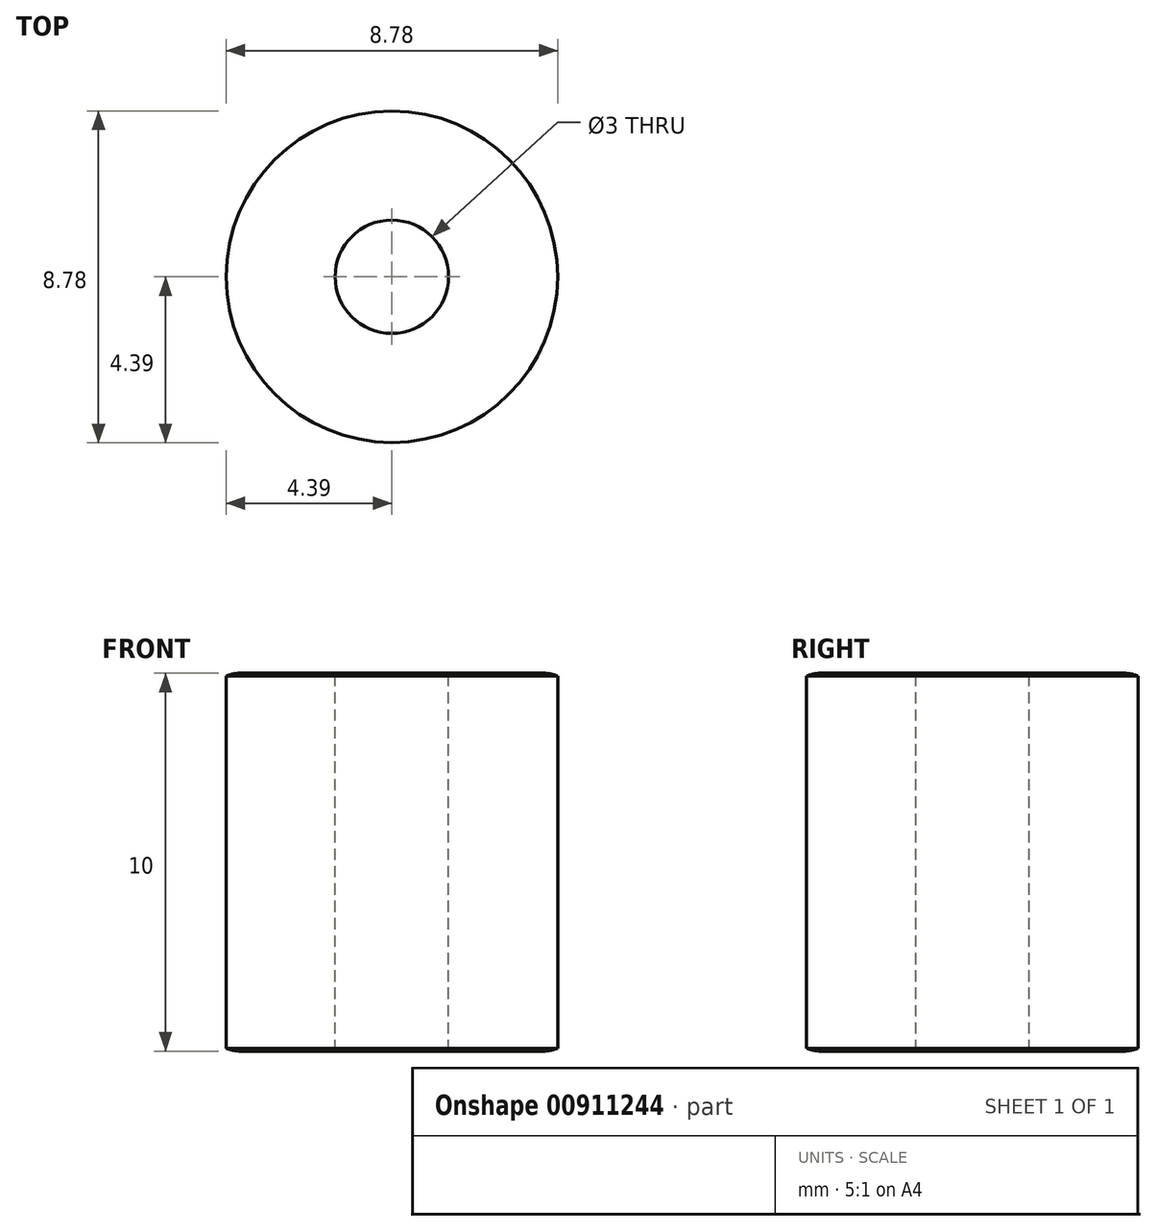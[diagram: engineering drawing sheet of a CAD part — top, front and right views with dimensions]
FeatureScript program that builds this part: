
annotation { "Feature Type Name" : "Feature", "Feature Type Description" : "" }
export const myFeature = defineFeature(function(context is Context, id is Id, definition is map)
    precondition{}
    {
        {
            var Q0;
            Q0=qCreatedBy(makeId("Top.planeOp"),FACE);
            var sketch = newSketch(context, id + "F0", { "sketchPlane" : qUnion([Q0])});
            skCircle(sketch, "E0", {"center": v(0, 0) * mm, "radius": 40 * mm});
            skCircle(sketch, "E1", {"center": v(0, 0) * mm, "radius": 35 * mm});
            skSolve(sketch);
        }
        {
            var Q0;
            Q0=qSketchRegion(id+"F0",true);
            extrude(context, id + "F1", {"entities" : qUnion([Q0]), "depth" : 10 * mm, "offsetDistance" : 25 * mm, "symmetric" : true});
        }
        {
            var Q0;
            Q0=makeQuery(id+"F1.opExtrude","CAP_EDGE",EDGE,{"disambiguationData":[OSD([sQuery(id+"F0.wireOp",EDGE,"E0")])],"isStart":false});
            var Q1;
            Q1=makeQuery(id+"F1.opExtrude","CAP_EDGE",EDGE,{"disambiguationData":[OSD([sQuery(id+"F0.wireOp",EDGE,"E0")])],"isStart":true});
            fillet(context, id + "F2", {"entities" : qUnion([Q0, Q1]), "radius" : 5 * mm, "tangentPropagation" : true, "allowEdgeOverflow" : false});
        }
        {
            var Q0;
            Q0=makeQuery(id+"F0.imprint","IMPRINT",FACE,{"disambiguationData":[TD([[makeQuery(id+"F0.imprint","IMPRINT",EDGE,{"derivedFrom":sQuery(id+"F0.wireOp",EDGE,"E1")}),1.0]])]});
            extrude(context, id + "F3", {"entities" : qUnion([Q0]), "operationType" : NewBodyOperationType.ADD, "depth" : 5 * mm, "offsetDistance" : 25 * mm, "symmetric" : true});
        }
        {
            var Q0;
            Q0=qCreatedBy(makeId("Top.planeOp"),FACE);
            var sketch = newSketch(context, id + "F4", { "sketchPlane" : qUnion([Q0])});
            skCircle(sketch, "E2", {"center": v(0, 0) * mm, "radius": 5 * mm});
            skSolve(sketch);
        }
        {
            var Q0;
            Q0=qSketchRegion(id+"F4",true);
            extrude(context, id + "F5", {"entities" : qUnion([Q0]), "operationType" : NewBodyOperationType.ADD, "depth" : 10 * mm, "offsetDistance" : 25 * mm, "symmetric" : true});
        }
        {
            var Q0;
            Q0=qCreatedBy(makeId("Top.planeOp"),FACE);
            var sketch = newSketch(context, id + "F6", { "sketchPlane" : qUnion([Q0])});
            skCircle(sketch, "E3", {"center": v(0, 0) * mm, "radius": 1.5 * mm});
            skSolve(sketch);
        }
        {
            var Q0;
            Q0=qSketchRegion(id+"F6",true);
            extrude(context, id + "F7", {"entities" : qUnion([Q0]), "operationType" : NewBodyOperationType.REMOVE, "oppositeDirection" : true, "depth" : 10 * mm, "offsetDistance" : 25 * mm, "symmetric" : true});
        }
        {
            var Q0;
            Q0=qCreatedBy(makeId("Top.planeOp"),FACE);
            var sketch = newSketch(context, id + "F8", { "sketchPlane" : qUnion([Q0])});
            skArc(sketch, "E4", {"start": v(-31.79, 5.48) * mm, "mid": v(-31.09, 8.72) * mm, "end": v(-30.01, 11.86) * mm});
            skLineSegment(sketch, "E5", {"start": v(-27.27, 12.9) * mm, "end": v(-8.35, 3.42) * mm});
            skLineSegment(sketch, "E6", {"start": v(-29.97, 3.18) * mm, "end": v(-8.88, 1.53) * mm});
            skArc(sketch, "E7.filletArc", {"start": v(-8.88, 1.53) * mm, "mid": v(-7.83, 2.26) * mm, "end": v(-8.35, 3.42) * mm});
            skPoint(sketch, "E8.visualSharp", {"position": v(-29.12, 13.82) * mm});
            skArc(sketch, "E8.filletArc", {"start": v(-27.27, 12.9) * mm, "mid": v(-28.87, 12.97) * mm, "end": v(-30.01, 11.86) * mm});
            skPoint(sketch, "E9.visualSharp", {"position": v(-32.04, 3.34) * mm});
            skArc(sketch, "E9.filletArc", {"start": v(-31.79, 5.48) * mm, "mid": v(-31.38, 3.93) * mm, "end": v(-29.97, 3.18) * mm});
            skPoint(sketch, "E10.1.0", {"position": v(-29.54, -13.16) * mm});
            skLineSegment(sketch, "E10.1.1", {"start": v(-27.66, -12.26) * mm, "end": v(-8.58, -3.14) * mm});
            skArc(sketch, "E10.1.2", {"start": v(-8.58, -3.14) * mm, "mid": v(-8.04, -1.99) * mm, "end": v(-9.07, -1.24) * mm});
            skLineSegment(sketch, "E10.1.3", {"start": v(-30.18, -2.5) * mm, "end": v(-9.07, -1.24) * mm});
            skPoint(sketch, "E10.1.4", {"position": v(-32.25, -2.63) * mm});
            skArc(sketch, "E10.1.5", {"start": v(-30.4, -11.18) * mm, "mid": v(-31.4, -8.02) * mm, "end": v(-32.05, -4.77) * mm});
            skArc(sketch, "E10.1.6", {"start": v(-30.18, -2.5) * mm, "mid": v(-31.6, -3.23) * mm, "end": v(-32.05, -4.77) * mm});
            skArc(sketch, "E10.1.7", {"start": v(-30.4, -11.18) * mm, "mid": v(-29.26, -12.32) * mm, "end": v(-27.66, -12.26) * mm});
            skPoint(sketch, "E10.2.0", {"position": v(-19.12, -26.2) * mm});
            skLineSegment(sketch, "E10.2.1", {"start": v(-17.95, -24.48) * mm, "end": v(-5.98, -7.04) * mm});
            skArc(sketch, "E10.2.2", {"start": v(-5.98, -7.04) * mm, "mid": v(-6.09, -5.77) * mm, "end": v(-7.35, -5.64) * mm});
            skLineSegment(sketch, "E10.2.3", {"start": v(-25.01, -17.29) * mm, "end": v(-7.35, -5.64) * mm});
            skPoint(sketch, "E10.2.4", {"position": v(-26.74, -18.43) * mm});
            skArc(sketch, "E10.2.5", {"start": v(-20.85, -24.9) * mm, "mid": v(-23.3, -22.68) * mm, "end": v(-25.5, -20.18) * mm});
            skArc(sketch, "E10.2.6", {"start": v(-25.01, -17.29) * mm, "mid": v(-25.88, -18.63) * mm, "end": v(-25.5, -20.18) * mm});
            skArc(sketch, "E10.2.7", {"start": v(-20.85, -24.9) * mm, "mid": v(-19.3, -25.33) * mm, "end": v(-17.95, -24.48) * mm});
            skPoint(sketch, "E10.center", {"position": v(0, -0.25) * mm});
            skPoint(sketch, "E11.0.3.0", {"position": v(-14.07, -29.37) * mm});
            skLineSegment(sketch, "E11.1.3.0", {"start": v(-3.43, -30.2) * mm, "end": v(-1.78, -9.12) * mm});
            skArc(sketch, "E11.4.3.0", {"start": v(-1.78, -9.12) * mm, "mid": v(-2.5, -8.08) * mm, "end": v(-3.67, -8.6) * mm});
            skLineSegment(sketch, "E11.8.3.0", {"start": v(-13.14, -27.5) * mm, "end": v(-3.67, -8.6) * mm});
            skPoint(sketch, "E11.11.3.0", {"position": v(-3.59, -32.28) * mm});
            skArc(sketch, "E11.12.3.0", {"start": v(-5.73, -32.03) * mm, "mid": v(-8.97, -31.33) * mm, "end": v(-12.1, -30.26) * mm});
            skArc(sketch, "E11.16.3.0", {"start": v(-13.14, -27.5) * mm, "mid": v(-13.22, -29.1) * mm, "end": v(-12.1, -30.26) * mm});
            skArc(sketch, "E11.20.3.0", {"start": v(-5.73, -32.03) * mm, "mid": v(-4.18, -31.62) * mm, "end": v(-3.43, -30.2) * mm});
            skPoint(sketch, "E11.0.4.0", {"position": v(2.38, -32.5) * mm});
            skLineSegment(sketch, "E11.1.4.0", {"start": v(12.01, -27.9) * mm, "end": v(2.9, -8.82) * mm});
            skArc(sketch, "E11.4.4.0", {"start": v(2.9, -8.82) * mm, "mid": v(1.74, -8.28) * mm, "end": v(1, -9.3) * mm});
            skLineSegment(sketch, "E11.8.4.0", {"start": v(2.25, -30.42) * mm, "end": v(1, -9.3) * mm});
            skPoint(sketch, "E11.11.4.0", {"position": v(12.9, -29.78) * mm});
            skArc(sketch, "E11.12.4.0", {"start": v(10.93, -30.63) * mm, "mid": v(7.77, -31.65) * mm, "end": v(4.52, -32.29) * mm});
            skArc(sketch, "E11.16.4.0", {"start": v(2.25, -30.42) * mm, "mid": v(2.98, -31.85) * mm, "end": v(4.52, -32.29) * mm});
            skArc(sketch, "E11.20.4.0", {"start": v(10.93, -30.63) * mm, "mid": v(12.07, -29.5) * mm, "end": v(12.01, -27.9) * mm});
            skPoint(sketch, "E12.0.5.0", {"position": v(18.18, -26.99) * mm});
            skLineSegment(sketch, "E12.1.5.0", {"start": v(24.23, -18.2) * mm, "end": v(6.8, -6.22) * mm});
            skArc(sketch, "E12.4.5.0", {"start": v(6.8, -6.22) * mm, "mid": v(5.53, -6.33) * mm, "end": v(5.4, -7.6) * mm});
            skLineSegment(sketch, "E12.8.5.0", {"start": v(17.04, -25.25) * mm, "end": v(5.4, -7.6) * mm});
            skPoint(sketch, "E12.11.5.0", {"position": v(25.94, -19.37) * mm});
            skArc(sketch, "E12.12.5.0", {"start": v(24.66, -21.1) * mm, "mid": v(22.43, -23.55) * mm, "end": v(19.94, -25.73) * mm});
            skArc(sketch, "E12.16.5.0", {"start": v(17.04, -25.25) * mm, "mid": v(18.38, -26.12) * mm, "end": v(19.94, -25.73) * mm});
            skArc(sketch, "E12.20.5.0", {"start": v(24.66, -21.1) * mm, "mid": v(25.08, -19.55) * mm, "end": v(24.23, -18.2) * mm});
            skPoint(sketch, "E13.0.6.0", {"position": v(29.12, -14.3) * mm});
            skLineSegment(sketch, "E13.1.6.0", {"start": v(29.96, -3.67) * mm, "end": v(8.87, -2.02) * mm});
            skArc(sketch, "E13.4.6.0", {"start": v(8.87, -2.02) * mm, "mid": v(7.83, -2.75) * mm, "end": v(8.34, -3.91) * mm});
            skLineSegment(sketch, "E13.8.6.0", {"start": v(27.26, -13.38) * mm, "end": v(8.34, -3.91) * mm});
            skPoint(sketch, "E13.11.6.0", {"position": v(32.03, -3.83) * mm});
            skArc(sketch, "E13.12.6.0", {"start": v(31.78, -5.97) * mm, "mid": v(31.08, -9.21) * mm, "end": v(30, -12.35) * mm});
            skArc(sketch, "E13.16.6.0", {"start": v(27.26, -13.38) * mm, "mid": v(28.86, -13.46) * mm, "end": v(30, -12.35) * mm});
            skArc(sketch, "E13.20.6.0", {"start": v(31.78, -5.97) * mm, "mid": v(31.37, -4.42) * mm, "end": v(29.96, -3.67) * mm});
            skPoint(sketch, "E14.0.7.0", {"position": v(32.25, 2.14) * mm});
            skLineSegment(sketch, "E14.1.7.0", {"start": v(27.66, 11.77) * mm, "end": v(8.57, 2.65) * mm});
            skArc(sketch, "E14.4.7.0", {"start": v(8.57, 2.65) * mm, "mid": v(8.03, 1.5) * mm, "end": v(9.06, 0.75) * mm});
            skLineSegment(sketch, "E14.8.7.0", {"start": v(30.18, 2.01) * mm, "end": v(9.06, 0.75) * mm});
            skPoint(sketch, "E14.11.7.0", {"position": v(29.53, 12.67) * mm});
            skArc(sketch, "E14.12.7.0", {"start": v(30.38, 10.69) * mm, "mid": v(31.4, 7.53) * mm, "end": v(32.04, 4.28) * mm});
            skArc(sketch, "E14.16.7.0", {"start": v(30.18, 2.01) * mm, "mid": v(31.6, 2.74) * mm, "end": v(32.04, 4.28) * mm});
            skArc(sketch, "E14.20.7.0", {"start": v(30.38, 10.69) * mm, "mid": v(29.26, 11.83) * mm, "end": v(27.66, 11.77) * mm});
            skPoint(sketch, "E15.0.8.0", {"position": v(26.74, 17.94) * mm});
            skLineSegment(sketch, "E15.1.8.0", {"start": v(17.94, 24) * mm, "end": v(5.97, 6.55) * mm});
            skArc(sketch, "E15.4.8.0", {"start": v(5.97, 6.55) * mm, "mid": v(6.08, 5.28) * mm, "end": v(7.35, 5.15) * mm});
            skLineSegment(sketch, "E15.8.8.0", {"start": v(25, 16.8) * mm, "end": v(7.35, 5.15) * mm});
            skPoint(sketch, "E15.11.8.0", {"position": v(19.12, 25.7) * mm});
            skArc(sketch, "E15.12.8.0", {"start": v(20.85, 24.42) * mm, "mid": v(23.3, 22.2) * mm, "end": v(25.48, 19.7) * mm});
            skArc(sketch, "E15.16.8.0", {"start": v(25, 16.8) * mm, "mid": v(25.88, 18.14) * mm, "end": v(25.48, 19.7) * mm});
            skArc(sketch, "E15.20.8.0", {"start": v(20.85, 24.42) * mm, "mid": v(19.3, 24.84) * mm, "end": v(17.94, 24) * mm});
            skPoint(sketch, "E15.0.9.0", {"position": v(14.06, 28.88) * mm});
            skLineSegment(sketch, "E15.1.9.0", {"start": v(3.42, 29.72) * mm, "end": v(1.77, 8.63) * mm});
            skArc(sketch, "E15.4.9.0", {"start": v(1.77, 8.63) * mm, "mid": v(2.5, 7.59) * mm, "end": v(3.67, 8.1) * mm});
            skLineSegment(sketch, "E15.8.9.0", {"start": v(13.13, 27.02) * mm, "end": v(3.67, 8.1) * mm});
            skPoint(sketch, "E15.11.9.0", {"position": v(3.58, 31.79) * mm});
            skArc(sketch, "E15.12.9.0", {"start": v(5.72, 31.54) * mm, "mid": v(8.96, 30.84) * mm, "end": v(12.1, 29.77) * mm});
            skArc(sketch, "E15.16.9.0", {"start": v(13.13, 27.02) * mm, "mid": v(13.22, 28.62) * mm, "end": v(12.1, 29.77) * mm});
            skArc(sketch, "E15.20.9.0", {"start": v(5.72, 31.54) * mm, "mid": v(4.17, 31.13) * mm, "end": v(3.42, 29.72) * mm});
            skPoint(sketch, "E15.0.10.0", {"position": v(-2.38, 32) * mm});
            skLineSegment(sketch, "E15.1.10.0", {"start": v(-12.02, 27.41) * mm, "end": v(-2.9, 8.33) * mm});
            skArc(sketch, "E15.4.10.0", {"start": v(-2.9, 8.33) * mm, "mid": v(-1.75, 7.79) * mm, "end": v(-1, 8.82) * mm});
            skLineSegment(sketch, "E15.8.10.0", {"start": v(-2.26, 29.93) * mm, "end": v(-1, 8.82) * mm});
            skPoint(sketch, "E15.11.10.0", {"position": v(-12.91, 29.29) * mm});
            skArc(sketch, "E15.12.10.0", {"start": v(-10.94, 30.14) * mm, "mid": v(-7.78, 31.16) * mm, "end": v(-4.53, 31.8) * mm});
            skArc(sketch, "E15.16.10.0", {"start": v(-2.26, 29.93) * mm, "mid": v(-2.99, 31.36) * mm, "end": v(-4.53, 31.8) * mm});
            skArc(sketch, "E15.20.10.0", {"start": v(-10.94, 30.14) * mm, "mid": v(-12.07, 29.01) * mm, "end": v(-12.02, 27.41) * mm});
            skPoint(sketch, "E15.0.11.0", {"position": v(-18.2, 26.5) * mm});
            skLineSegment(sketch, "E15.1.11.0", {"start": v(-24.24, 17.7) * mm, "end": v(-6.8, 5.73) * mm});
            skArc(sketch, "E15.4.11.0", {"start": v(-6.8, 5.73) * mm, "mid": v(-5.53, 5.84) * mm, "end": v(-5.4, 7.1) * mm});
            skLineSegment(sketch, "E15.8.11.0", {"start": v(-17.05, 24.76) * mm, "end": v(-5.4, 7.1) * mm});
            skPoint(sketch, "E15.11.11.0", {"position": v(-25.95, 18.88) * mm});
            skArc(sketch, "E15.12.11.0", {"start": v(-24.67, 20.6) * mm, "mid": v(-22.44, 23.06) * mm, "end": v(-19.94, 25.24) * mm});
            skArc(sketch, "E15.16.11.0", {"start": v(-17.05, 24.76) * mm, "mid": v(-18.39, 25.63) * mm, "end": v(-19.94, 25.24) * mm});
            skArc(sketch, "E15.20.11.0", {"start": v(-24.67, 20.6) * mm, "mid": v(-25.09, 19.06) * mm, "end": v(-24.24, 17.7) * mm});
            skSolve(sketch);
        }
        {
            var Q0;
            Q0=qSketchRegion(id+"F8",true);
            extrude(context, id + "F9", {"entities" : qUnion([Q0]), "operationType" : NewBodyOperationType.REMOVE, "oppositeDirection" : true, "depth" : 5 * mm, "offsetDistance" : 25 * mm, "symmetric" : true});
        }
        {
            var Q0;
            Q0=makeQuery(id+"F9.boolean.opBoolean","COPY",EDGE,{"derivedFrom":makeQuery(id+"F9.opExtrude","CAP_EDGE",EDGE,{"disambiguationData":[OSD([sQuery(id+"F8.wireOp",EDGE,"E6")])],"isStart":true})});
            var Q1;
            Q1=makeQuery(id+"F9.boolean.opBoolean","COPY",EDGE,{"derivedFrom":makeQuery(id+"F9.opExtrude","CAP_EDGE",EDGE,{"disambiguationData":[OSD([sQuery(id+"F8.wireOp",EDGE,"E5")])],"isStart":true})});
            var Q2;
            Q2=makeQuery(id+"F3.opExtrude","CAP_EDGE",EDGE,{"disambiguationData":[OSD([sQuery(id+"F0.wireOp",EDGE,"E1")])],"isStart":true});
            var Q3;
            Q3=makeQuery(id+"F2.opFillet","BLEND_EDGE",EDGE,{"blendedFrom":[makeQuery(id+"F1.opExtrude","CAP_EDGE",EDGE,{"disambiguationData":[OSD([sQuery(id+"F0.wireOp",EDGE,"E0")])],"isStart":true}),makeQuery(id+"F1.opExtrude","SWEPT_FACE",FACE,{"disambiguationData":[OSD([sQuery(id+"F0.wireOp",EDGE,"E1")])]})],"blendedInto":[makeQuery(id+"F1.opExtrude","SWEPT_FACE",FACE,{"disambiguationData":[OSD([sQuery(id+"F0.wireOp",EDGE,"E1")])]})]});
            var Q4;
            Q4=makeQuery(id+"F9.boolean.opBoolean","COPY",EDGE,{"derivedFrom":makeQuery(id+"F9.opExtrude","CAP_EDGE",EDGE,{"disambiguationData":[OSD([sQuery(id+"F8.wireOp",EDGE,"E15.12.8.0")])],"isStart":false})});
            var Q5;
            Q5=makeQuery(id+"F9.boolean.opBoolean","COPY",EDGE,{"derivedFrom":makeQuery(id+"F9.opExtrude","CAP_EDGE",EDGE,{"disambiguationData":[OSD([sQuery(id+"F8.wireOp",EDGE,"E11.12.4.0")])],"isStart":false})});
            var Q6;
            Q6=makeQuery(id+"F9.boolean.opBoolean","COPY",EDGE,{"derivedFrom":makeQuery(id+"F9.opExtrude","CAP_EDGE",EDGE,{"disambiguationData":[OSD([sQuery(id+"F8.wireOp",EDGE,"E12.1.5.0")])],"isStart":false})});
            var Q7;
            Q7=makeQuery(id+"F9.boolean.opBoolean","COPY",EDGE,{"derivedFrom":makeQuery(id+"F9.opExtrude","CAP_EDGE",EDGE,{"disambiguationData":[OSD([sQuery(id+"F8.wireOp",EDGE,"E12.8.5.0")])],"isStart":false})});
            var Q8;
            Q8=makeQuery(id+"F9.boolean.opBoolean","COPY",EDGE,{"derivedFrom":makeQuery(id+"F9.opExtrude","CAP_EDGE",EDGE,{"disambiguationData":[OSD([sQuery(id+"F8.wireOp",EDGE,"E12.20.5.0")])],"isStart":false})});
            var Q9;
            Q9=makeQuery(id+"F9.boolean.opBoolean","COPY",EDGE,{"derivedFrom":makeQuery(id+"F9.opExtrude","CAP_EDGE",EDGE,{"disambiguationData":[OSD([sQuery(id+"F8.wireOp",EDGE,"E13.8.6.0")])],"isStart":false})});
            var Q10;
            Q10=makeQuery(id+"F9.boolean.opBoolean","COPY",EDGE,{"derivedFrom":makeQuery(id+"F9.opExtrude","CAP_EDGE",EDGE,{"disambiguationData":[OSD([sQuery(id+"F8.wireOp",EDGE,"E11.8.3.0")])],"isStart":false})});
            var Q11;
            Q11=makeQuery(id+"F9.boolean.opBoolean","COPY",EDGE,{"derivedFrom":makeQuery(id+"F9.opExtrude","CAP_EDGE",EDGE,{"disambiguationData":[OSD([sQuery(id+"F8.wireOp",EDGE,"E11.12.3.0")])],"isStart":false})});
            var Q12;
            Q12=makeQuery(id+"F9.boolean.opBoolean","COPY",EDGE,{"derivedFrom":makeQuery(id+"F9.opExtrude","CAP_EDGE",EDGE,{"disambiguationData":[OSD([sQuery(id+"F8.wireOp",EDGE,"E11.1.4.0")])],"isStart":false})});
            var Q13;
            Q13=makeQuery(id+"F9.boolean.opBoolean","COPY",EDGE,{"derivedFrom":makeQuery(id+"F9.opExtrude","CAP_EDGE",EDGE,{"disambiguationData":[OSD([sQuery(id+"F8.wireOp",EDGE,"E15.20.11.0")])],"isStart":false})});
            var Q14;
            Q14=makeQuery(id+"F9.boolean.opBoolean","COPY",EDGE,{"derivedFrom":makeQuery(id+"F9.opExtrude","CAP_EDGE",EDGE,{"disambiguationData":[OSD([sQuery(id+"F8.wireOp",EDGE,"E15.20.10.0")])],"isStart":false})});
            var Q15;
            Q15=makeQuery(id+"F9.boolean.opBoolean","COPY",EDGE,{"derivedFrom":makeQuery(id+"F9.opExtrude","CAP_EDGE",EDGE,{"disambiguationData":[OSD([sQuery(id+"F8.wireOp",EDGE,"E10.2.5")])],"isStart":false})});
            var Q16;
            Q16=makeQuery(id+"F9.boolean.opBoolean","COPY",EDGE,{"derivedFrom":makeQuery(id+"F9.opExtrude","CAP_EDGE",EDGE,{"disambiguationData":[OSD([sQuery(id+"F8.wireOp",EDGE,"E10.2.3")])],"isStart":false})});
            var Q17;
            Q17=makeQuery(id+"F9.boolean.opBoolean","COPY",EDGE,{"derivedFrom":makeQuery(id+"F9.opExtrude","CAP_EDGE",EDGE,{"disambiguationData":[OSD([sQuery(id+"F8.wireOp",EDGE,"E4")])],"isStart":false})});
            var Q18;
            Q18=makeQuery(id+"F9.boolean.opBoolean","COPY",EDGE,{"derivedFrom":makeQuery(id+"F9.opExtrude","CAP_EDGE",EDGE,{"disambiguationData":[OSD([sQuery(id+"F8.wireOp",EDGE,"E10.2.1")])],"isStart":false})});
            var Q19;
            Q19=makeQuery(id+"F9.boolean.opBoolean","COPY",EDGE,{"derivedFrom":makeQuery(id+"F9.opExtrude","CAP_EDGE",EDGE,{"disambiguationData":[OSD([sQuery(id+"F8.wireOp",EDGE,"E10.1.7")])],"isStart":false})});
            var Q20;
            Q20=makeQuery(id+"F9.boolean.opBoolean","COPY",EDGE,{"derivedFrom":makeQuery(id+"F9.opExtrude","CAP_EDGE",EDGE,{"disambiguationData":[OSD([sQuery(id+"F8.wireOp",EDGE,"E10.1.5")])],"isStart":false})});
            var Q21;
            Q21=makeQuery(id+"F9.boolean.opBoolean","COPY",EDGE,{"derivedFrom":makeQuery(id+"F9.opExtrude","CAP_EDGE",EDGE,{"disambiguationData":[OSD([sQuery(id+"F8.wireOp",EDGE,"E10.1.1")])],"isStart":false})});
            var Q22;
            Q22=makeQuery(id+"F9.boolean.opBoolean","COPY",EDGE,{"derivedFrom":makeQuery(id+"F9.opExtrude","CAP_EDGE",EDGE,{"disambiguationData":[OSD([sQuery(id+"F8.wireOp",EDGE,"E15.12.11.0")])],"isStart":false})});
            var Q23;
            Q23=makeQuery(id+"F9.boolean.opBoolean","COPY",EDGE,{"derivedFrom":makeQuery(id+"F9.opExtrude","CAP_EDGE",EDGE,{"disambiguationData":[OSD([sQuery(id+"F8.wireOp",EDGE,"E5")])],"isStart":false})});
            var Q24;
            Q24=makeQuery(id+"F9.boolean.opBoolean","COPY",EDGE,{"derivedFrom":makeQuery(id+"F9.opExtrude","CAP_EDGE",EDGE,{"disambiguationData":[OSD([sQuery(id+"F8.wireOp",EDGE,"E15.8.11.0")])],"isStart":false})});
            var Q25;
            Q25=makeQuery(id+"F9.boolean.opBoolean","COPY",EDGE,{"derivedFrom":makeQuery(id+"F9.opExtrude","CAP_EDGE",EDGE,{"disambiguationData":[OSD([sQuery(id+"F8.wireOp",EDGE,"E15.12.9.0")])],"isStart":false})});
            var Q26;
            Q26=makeQuery(id+"F9.boolean.opBoolean","COPY",EDGE,{"derivedFrom":makeQuery(id+"F9.opExtrude","CAP_EDGE",EDGE,{"disambiguationData":[OSD([sQuery(id+"F8.wireOp",EDGE,"E15.8.8.0")])],"isStart":false})});
            var Q27;
            Q27=makeQuery(id+"F9.boolean.opBoolean","COPY",EDGE,{"derivedFrom":makeQuery(id+"F9.opExtrude","CAP_EDGE",EDGE,{"disambiguationData":[OSD([sQuery(id+"F8.wireOp",EDGE,"E13.12.6.0")])],"isStart":false})});
            var Q28;
            Q28=makeQuery(id+"F9.boolean.opBoolean","COPY",EDGE,{"derivedFrom":makeQuery(id+"F9.opExtrude","CAP_EDGE",EDGE,{"disambiguationData":[OSD([sQuery(id+"F8.wireOp",EDGE,"E12.16.5.0")])],"isStart":false})});
            var Q29;
            Q29=makeQuery(id+"F9.boolean.opBoolean","COPY",EDGE,{"derivedFrom":makeQuery(id+"F9.opExtrude","CAP_EDGE",EDGE,{"disambiguationData":[OSD([sQuery(id+"F8.wireOp",EDGE,"E14.1.7.0")])],"isStart":false})});
            var Q30;
            Q30=makeQuery(id+"F9.boolean.opBoolean","COPY",EDGE,{"derivedFrom":makeQuery(id+"F9.opExtrude","CAP_EDGE",EDGE,{"disambiguationData":[OSD([sQuery(id+"F8.wireOp",EDGE,"E14.12.7.0")])],"isStart":false})});
            var Q31;
            Q31=makeQuery(id+"F9.boolean.opBoolean","COPY",EDGE,{"derivedFrom":makeQuery(id+"F9.opExtrude","CAP_EDGE",EDGE,{"disambiguationData":[OSD([sQuery(id+"F8.wireOp",EDGE,"E15.1.8.0")])],"isStart":false})});
            var Q32;
            Q32=makeQuery(id+"F9.boolean.opBoolean","COPY",EDGE,{"derivedFrom":makeQuery(id+"F9.opExtrude","CAP_EDGE",EDGE,{"disambiguationData":[OSD([sQuery(id+"F8.wireOp",EDGE,"E15.4.9.0")])],"isStart":false})});
            var Q33;
            Q33=makeQuery(id+"F9.boolean.opBoolean","COPY",EDGE,{"derivedFrom":makeQuery(id+"F9.opExtrude","CAP_EDGE",EDGE,{"disambiguationData":[OSD([sQuery(id+"F8.wireOp",EDGE,"E15.12.10.0")])],"isStart":false})});
            var Q34;
            Q34=makeQuery(id+"F9.boolean.opBoolean","COPY",EDGE,{"derivedFrom":makeQuery(id+"F9.opExtrude","CAP_EDGE",EDGE,{"disambiguationData":[OSD([sQuery(id+"F8.wireOp",EDGE,"E12.12.5.0")])],"isStart":false})});
            var Q35;
            Q35=makeQuery(id+"F9.boolean.opBoolean","COPY",EDGE,{"derivedFrom":makeQuery(id+"F9.opExtrude","CAP_EDGE",EDGE,{"disambiguationData":[OSD([sQuery(id+"F8.wireOp",EDGE,"E15.16.10.0")])],"isStart":false})});
            var Q36;
            Q36=makeQuery(id+"F9.boolean.opBoolean","COPY",EDGE,{"derivedFrom":makeQuery(id+"F9.opExtrude","CAP_EDGE",EDGE,{"disambiguationData":[OSD([sQuery(id+"F8.wireOp",EDGE,"E11.16.3.0")])],"isStart":false})});
            var Q37;
            Q37=makeQuery(id+"F9.boolean.opBoolean","COPY",EDGE,{"derivedFrom":makeQuery(id+"F9.opExtrude","CAP_EDGE",EDGE,{"disambiguationData":[OSD([sQuery(id+"F8.wireOp",EDGE,"E15.1.10.0")])],"isStart":false})});
            var Q38;
            Q38=makeQuery(id+"F9.boolean.opBoolean","COPY",EDGE,{"derivedFrom":makeQuery(id+"F9.opExtrude","CAP_EDGE",EDGE,{"disambiguationData":[OSD([sQuery(id+"F8.wireOp",EDGE,"E10.2.6")])],"isStart":false})});
            var Q39;
            Q39=makeQuery(id+"F9.boolean.opBoolean","COPY",EDGE,{"derivedFrom":makeQuery(id+"F9.opExtrude","CAP_EDGE",EDGE,{"disambiguationData":[OSD([sQuery(id+"F8.wireOp",EDGE,"E15.8.9.0")])],"isStart":false})});
            var Q40;
            Q40=makeQuery(id+"F5.opExtrude","CAP_EDGE",EDGE,{"disambiguationData":[OSD([sQuery(id+"F4.wireOp",EDGE,"E2")])],"isStart":true});
            var Q41;
            Q41=makeQuery(id+"F2.opFillet","BLEND_EDGE",EDGE,{"blendedFrom":[makeQuery(id+"F1.opExtrude","CAP_EDGE",EDGE,{"disambiguationData":[OSD([sQuery(id+"F0.wireOp",EDGE,"E0")])],"isStart":false}),makeQuery(id+"F1.opExtrude","SWEPT_FACE",FACE,{"disambiguationData":[OSD([sQuery(id+"F0.wireOp",EDGE,"E1")])]})],"blendedInto":[makeQuery(id+"F1.opExtrude","SWEPT_FACE",FACE,{"disambiguationData":[OSD([sQuery(id+"F0.wireOp",EDGE,"E1")])]})]});
            var Q42;
            Q42=makeQuery(id+"F9.boolean.opBoolean","COPY",EDGE,{"derivedFrom":makeQuery(id+"F9.opExtrude","CAP_EDGE",EDGE,{"disambiguationData":[OSD([sQuery(id+"F8.wireOp",EDGE,"E15.8.8.0")])],"isStart":true})});
            var Q43;
            Q43=makeQuery(id+"F9.boolean.opBoolean","COPY",EDGE,{"derivedFrom":makeQuery(id+"F9.opExtrude","CAP_EDGE",EDGE,{"disambiguationData":[OSD([sQuery(id+"F8.wireOp",EDGE,"E15.16.8.0")])],"isStart":false})});
            var Q44;
            Q44=makeQuery(id+"F9.boolean.opBoolean","COPY",EDGE,{"derivedFrom":makeQuery(id+"F9.opExtrude","CAP_EDGE",EDGE,{"disambiguationData":[OSD([sQuery(id+"F8.wireOp",EDGE,"E11.1.3.0")])],"isStart":false})});
            var Q45;
            Q45=makeQuery(id+"F9.boolean.opBoolean","COPY",EDGE,{"derivedFrom":makeQuery(id+"F9.opExtrude","CAP_EDGE",EDGE,{"disambiguationData":[OSD([sQuery(id+"F8.wireOp",EDGE,"E11.8.4.0")])],"isStart":true})});
            var Q46;
            Q46=makeQuery(id+"F9.boolean.opBoolean","COPY",EDGE,{"derivedFrom":makeQuery(id+"F9.opExtrude","CAP_EDGE",EDGE,{"disambiguationData":[OSD([sQuery(id+"F8.wireOp",EDGE,"E11.8.4.0")])],"isStart":false})});
            var Q47;
            Q47=makeQuery(id+"F9.boolean.opBoolean","COPY",EDGE,{"derivedFrom":makeQuery(id+"F9.opExtrude","CAP_EDGE",EDGE,{"disambiguationData":[OSD([sQuery(id+"F8.wireOp",EDGE,"E11.12.4.0")])],"isStart":true})});
            var Q48;
            Q48=makeQuery(id+"F9.boolean.opBoolean","COPY",EDGE,{"derivedFrom":makeQuery(id+"F9.opExtrude","CAP_EDGE",EDGE,{"disambiguationData":[OSD([sQuery(id+"F8.wireOp",EDGE,"E12.8.5.0")])],"isStart":true})});
            var Q49;
            Q49=makeQuery(id+"F9.boolean.opBoolean","COPY",EDGE,{"derivedFrom":makeQuery(id+"F9.opExtrude","CAP_EDGE",EDGE,{"disambiguationData":[OSD([sQuery(id+"F8.wireOp",EDGE,"E13.20.6.0")])],"isStart":false})});
            var Q50;
            Q50=makeQuery(id+"F9.boolean.opBoolean","COPY",EDGE,{"derivedFrom":makeQuery(id+"F9.opExtrude","CAP_EDGE",EDGE,{"disambiguationData":[OSD([sQuery(id+"F8.wireOp",EDGE,"E14.8.7.0")])],"isStart":false})});
            var Q51;
            Q51=makeQuery(id+"F9.boolean.opBoolean","COPY",EDGE,{"derivedFrom":makeQuery(id+"F9.opExtrude","CAP_EDGE",EDGE,{"disambiguationData":[OSD([sQuery(id+"F8.wireOp",EDGE,"E14.20.7.0")])],"isStart":false})});
            var Q52;
            Q52=makeQuery(id+"F9.boolean.opBoolean","COPY",EDGE,{"derivedFrom":makeQuery(id+"F9.opExtrude","CAP_EDGE",EDGE,{"disambiguationData":[OSD([sQuery(id+"F8.wireOp",EDGE,"E11.8.3.0")])],"isStart":true})});
            var Q53;
            Q53=makeQuery(id+"F9.boolean.opBoolean","COPY",EDGE,{"derivedFrom":makeQuery(id+"F9.opExtrude","SWEPT_EDGE",EDGE,{"disambiguationData":[OSD([sQuery(id+"F8.wireOp",EDGE,"E15.12.11.0"),sQuery(id+"F8.wireOp",EDGE,"E15.16.11.0")])]})});
            var Q54;
            Q54=makeQuery(id+"F3.opExtrude","CAP_EDGE",EDGE,{"disambiguationData":[OSD([sQuery(id+"F0.wireOp",EDGE,"E1")])],"isStart":false});
            var Q55;
            Q55=makeQuery(id+"F9.boolean.opBoolean","COPY",EDGE,{"derivedFrom":makeQuery(id+"F9.opExtrude","CAP_EDGE",EDGE,{"disambiguationData":[OSD([sQuery(id+"F8.wireOp",EDGE,"E11.12.3.0")])],"isStart":true})});
            var Q56;
            Q56=makeQuery(id+"F9.boolean.opBoolean","COPY",EDGE,{"derivedFrom":makeQuery(id+"F9.opExtrude","CAP_EDGE",EDGE,{"disambiguationData":[OSD([sQuery(id+"F8.wireOp",EDGE,"E11.20.3.0")])],"isStart":false})});
            var Q57;
            Q57=makeQuery(id+"F9.boolean.opBoolean","COPY",EDGE,{"derivedFrom":makeQuery(id+"F9.opExtrude","CAP_EDGE",EDGE,{"disambiguationData":[OSD([sQuery(id+"F8.wireOp",EDGE,"E11.1.4.0")])],"isStart":true})});
            var Q58;
            Q58=makeQuery(id+"F9.boolean.opBoolean","COPY",EDGE,{"derivedFrom":makeQuery(id+"F9.opExtrude","CAP_EDGE",EDGE,{"disambiguationData":[OSD([sQuery(id+"F8.wireOp",EDGE,"E15.8.11.0")])],"isStart":true})});
            var Q59;
            Q59=makeQuery(id+"F9.boolean.opBoolean","COPY",EDGE,{"derivedFrom":makeQuery(id+"F9.opExtrude","CAP_EDGE",EDGE,{"disambiguationData":[OSD([sQuery(id+"F8.wireOp",EDGE,"E15.1.11.0")])],"isStart":false})});
            var Q60;
            Q60=makeQuery(id+"F9.boolean.opBoolean","COPY",EDGE,{"derivedFrom":makeQuery(id+"F9.opExtrude","CAP_EDGE",EDGE,{"disambiguationData":[OSD([sQuery(id+"F8.wireOp",EDGE,"E15.4.11.0")])],"isStart":false})});
            var Q61;
            Q61=makeQuery(id+"F9.boolean.opBoolean","COPY",EDGE,{"derivedFrom":makeQuery(id+"F9.opExtrude","CAP_EDGE",EDGE,{"disambiguationData":[OSD([sQuery(id+"F8.wireOp",EDGE,"E8.filletArc")])],"isStart":false})});
            var Q62;
            Q62=makeQuery(id+"F9.boolean.opBoolean","COPY",EDGE,{"derivedFrom":makeQuery(id+"F9.opExtrude","CAP_EDGE",EDGE,{"disambiguationData":[OSD([sQuery(id+"F8.wireOp",EDGE,"E15.1.11.0")])],"isStart":true})});
            var Q63;
            Q63=makeQuery(id+"F9.boolean.opBoolean","COPY",EDGE,{"derivedFrom":makeQuery(id+"F9.opExtrude","CAP_EDGE",EDGE,{"disambiguationData":[OSD([sQuery(id+"F8.wireOp",EDGE,"E10.2.6")])],"isStart":true})});
            var Q64;
            Q64=makeQuery(id+"F9.boolean.opBoolean","COPY",EDGE,{"derivedFrom":makeQuery(id+"F9.opExtrude","SWEPT_EDGE",EDGE,{"disambiguationData":[OSD([sQuery(id+"F8.wireOp",EDGE,"E12.1.5.0"),sQuery(id+"F8.wireOp",EDGE,"E12.20.5.0")])]})});
            var Q65;
            Q65=makeQuery(id+"F9.boolean.opBoolean","COPY",EDGE,{"derivedFrom":makeQuery(id+"F9.opExtrude","SWEPT_EDGE",EDGE,{"disambiguationData":[OSD([sQuery(id+"F8.wireOp",EDGE,"E11.12.4.0"),sQuery(id+"F8.wireOp",EDGE,"E11.16.4.0")])]})});
            var Q66;
            Q66=makeQuery(id+"F9.boolean.opBoolean","COPY",EDGE,{"derivedFrom":makeQuery(id+"F9.opExtrude","CAP_EDGE",EDGE,{"disambiguationData":[OSD([sQuery(id+"F8.wireOp",EDGE,"E10.2.5")])],"isStart":true})});
            var Q67;
            Q67=makeQuery(id+"F9.boolean.opBoolean","COPY",EDGE,{"derivedFrom":makeQuery(id+"F9.opExtrude","SWEPT_EDGE",EDGE,{"disambiguationData":[OSD([sQuery(id+"F8.wireOp",EDGE,"E11.12.4.0"),sQuery(id+"F8.wireOp",EDGE,"E11.20.4.0")])]})});
            var Q68;
            Q68=makeQuery(id+"F9.boolean.opBoolean","COPY",EDGE,{"derivedFrom":makeQuery(id+"F9.opExtrude","CAP_EDGE",EDGE,{"disambiguationData":[OSD([sQuery(id+"F8.wireOp",EDGE,"E10.2.3")])],"isStart":true})});
            var Q69;
            Q69=makeQuery(id+"F9.boolean.opBoolean","COPY",EDGE,{"derivedFrom":makeQuery(id+"F9.opExtrude","CAP_EDGE",EDGE,{"disambiguationData":[OSD([sQuery(id+"F8.wireOp",EDGE,"E10.2.2")])],"isStart":false})});
            var Q70;
            Q70=makeQuery(id+"F9.boolean.opBoolean","COPY",EDGE,{"derivedFrom":makeQuery(id+"F9.opExtrude","SWEPT_EDGE",EDGE,{"disambiguationData":[OSD([sQuery(id+"F8.wireOp",EDGE,"E15.12.9.0"),sQuery(id+"F8.wireOp",EDGE,"E15.20.9.0")])]})});
            var Q71;
            Q71=makeQuery(id+"F9.boolean.opBoolean","COPY",EDGE,{"derivedFrom":makeQuery(id+"F9.opExtrude","SWEPT_EDGE",EDGE,{"disambiguationData":[OSD([sQuery(id+"F8.wireOp",EDGE,"E11.12.3.0"),sQuery(id+"F8.wireOp",EDGE,"E11.16.3.0")])]})});
            var Q72;
            Q72=makeQuery(id+"F9.boolean.opBoolean","COPY",EDGE,{"derivedFrom":makeQuery(id+"F9.opExtrude","CAP_EDGE",EDGE,{"disambiguationData":[OSD([sQuery(id+"F8.wireOp",EDGE,"E10.2.1")])],"isStart":true})});
            var Q73;
            Q73=makeQuery(id+"F9.boolean.opBoolean","COPY",EDGE,{"derivedFrom":makeQuery(id+"F9.opExtrude","CAP_EDGE",EDGE,{"disambiguationData":[OSD([sQuery(id+"F8.wireOp",EDGE,"E10.1.6")])],"isStart":false})});
            var Q74;
            Q74=makeQuery(id+"F9.boolean.opBoolean","COPY",EDGE,{"derivedFrom":makeQuery(id+"F9.opExtrude","SWEPT_EDGE",EDGE,{"disambiguationData":[OSD([sQuery(id+"F8.wireOp",EDGE,"E15.12.8.0"),sQuery(id+"F8.wireOp",EDGE,"E15.20.8.0")])]})});
            var Q75;
            Q75=makeQuery(id+"F9.boolean.opBoolean","COPY",EDGE,{"derivedFrom":makeQuery(id+"F9.opExtrude","CAP_EDGE",EDGE,{"disambiguationData":[OSD([sQuery(id+"F8.wireOp",EDGE,"E10.1.5")])],"isStart":true})});
            var Q76;
            Q76=makeQuery(id+"F9.boolean.opBoolean","COPY",EDGE,{"derivedFrom":makeQuery(id+"F9.opExtrude","CAP_EDGE",EDGE,{"disambiguationData":[OSD([sQuery(id+"F8.wireOp",EDGE,"E10.1.3")])],"isStart":false})});
            var Q77;
            Q77=makeQuery(id+"F9.boolean.opBoolean","COPY",EDGE,{"derivedFrom":makeQuery(id+"F9.opExtrude","CAP_EDGE",EDGE,{"disambiguationData":[OSD([sQuery(id+"F8.wireOp",EDGE,"E10.1.2")])],"isStart":false})});
            var Q78;
            Q78=makeQuery(id+"F9.boolean.opBoolean","COPY",EDGE,{"derivedFrom":makeQuery(id+"F9.opExtrude","CAP_EDGE",EDGE,{"disambiguationData":[OSD([sQuery(id+"F8.wireOp",EDGE,"E4")])],"isStart":true})});
            var Q79;
            Q79=makeQuery(id+"F9.boolean.opBoolean","COPY",EDGE,{"derivedFrom":makeQuery(id+"F9.opExtrude","CAP_EDGE",EDGE,{"disambiguationData":[OSD([sQuery(id+"F8.wireOp",EDGE,"E15.20.11.0")])],"isStart":true})});
            var Q80;
            Q80=makeQuery(id+"F9.boolean.opBoolean","COPY",EDGE,{"derivedFrom":makeQuery(id+"F9.opExtrude","CAP_EDGE",EDGE,{"disambiguationData":[OSD([sQuery(id+"F8.wireOp",EDGE,"E15.16.11.0")])],"isStart":false})});
            var Q81;
            Q81=makeQuery(id+"F9.boolean.opBoolean","COPY",EDGE,{"derivedFrom":makeQuery(id+"F9.opExtrude","CAP_EDGE",EDGE,{"disambiguationData":[OSD([sQuery(id+"F8.wireOp",EDGE,"E15.12.11.0")])],"isStart":true})});
            var Q82;
            Q82=makeQuery(id+"F9.boolean.opBoolean","COPY",EDGE,{"derivedFrom":makeQuery(id+"F9.opExtrude","SWEPT_EDGE",EDGE,{"disambiguationData":[OSD([sQuery(id+"F8.wireOp",EDGE,"E12.4.5.0"),sQuery(id+"F8.wireOp",EDGE,"E12.8.5.0")])]})});
            var Q83;
            Q83=makeQuery(id+"F9.boolean.opBoolean","COPY",EDGE,{"derivedFrom":makeQuery(id+"F9.opExtrude","SWEPT_EDGE",EDGE,{"disambiguationData":[OSD([sQuery(id+"F8.wireOp",EDGE,"E12.8.5.0"),sQuery(id+"F8.wireOp",EDGE,"E12.16.5.0")])]})});
            var Q84;
            Q84=makeQuery(id+"F9.boolean.opBoolean","COPY",EDGE,{"derivedFrom":makeQuery(id+"F9.opExtrude","CAP_EDGE",EDGE,{"disambiguationData":[OSD([sQuery(id+"F8.wireOp",EDGE,"E9.filletArc")])],"isStart":false})});
            var Q85;
            Q85=makeQuery(id+"F9.boolean.opBoolean","COPY",EDGE,{"derivedFrom":makeQuery(id+"F9.opExtrude","SWEPT_EDGE",EDGE,{"disambiguationData":[OSD([sQuery(id+"F8.wireOp",EDGE,"E12.12.5.0"),sQuery(id+"F8.wireOp",EDGE,"E12.20.5.0")])]})});
            var Q86;
            Q86=makeQuery(id+"F9.boolean.opBoolean","COPY",EDGE,{"derivedFrom":makeQuery(id+"F9.opExtrude","SWEPT_EDGE",EDGE,{"disambiguationData":[OSD([sQuery(id+"F8.wireOp",EDGE,"E12.12.5.0"),sQuery(id+"F8.wireOp",EDGE,"E12.16.5.0")])]})});
            var Q87;
            Q87=makeQuery(id+"F9.boolean.opBoolean","COPY",EDGE,{"derivedFrom":makeQuery(id+"F9.opExtrude","SWEPT_EDGE",EDGE,{"disambiguationData":[OSD([sQuery(id+"F8.wireOp",EDGE,"E13.8.6.0"),sQuery(id+"F8.wireOp",EDGE,"E13.16.6.0")])]})});
            var Q88;
            Q88=makeQuery(id+"F5.boolean.opBoolean","INTERSECT",EDGE,{"derivedFrom":[makeQuery(id+"F3.opExtrude","CAP_FACE",FACE,{"disambiguationData":[OSD([sQuery(id+"F0.wireOp",EDGE,"E1")])],"isStart":false}),makeQuery(id+"F5.opExtrude","SWEPT_FACE",FACE,{"disambiguationData":[OSD([sQuery(id+"F4.wireOp",EDGE,"E2")])]})]});
            var Q89;
            Q89=makeQuery(id+"F9.boolean.opBoolean","COPY",EDGE,{"derivedFrom":makeQuery(id+"F9.opExtrude","CAP_EDGE",EDGE,{"disambiguationData":[OSD([sQuery(id+"F8.wireOp",EDGE,"E15.1.10.0")])],"isStart":true})});
            var Q90;
            Q90=makeQuery(id+"F9.boolean.opBoolean","COPY",EDGE,{"derivedFrom":makeQuery(id+"F9.opExtrude","SWEPT_EDGE",EDGE,{"disambiguationData":[OSD([sQuery(id+"F8.wireOp",EDGE,"E4"),sQuery(id+"F8.wireOp",EDGE,"E8.filletArc")])]})});
            var Q91;
            Q91=makeQuery(id+"F9.boolean.opBoolean","COPY",EDGE,{"derivedFrom":makeQuery(id+"F9.opExtrude","CAP_EDGE",EDGE,{"disambiguationData":[OSD([sQuery(id+"F8.wireOp",EDGE,"E15.20.9.0")])],"isStart":false})});
            var Q92;
            Q92=makeQuery(id+"F9.boolean.opBoolean","COPY",EDGE,{"derivedFrom":makeQuery(id+"F9.opExtrude","CAP_EDGE",EDGE,{"disambiguationData":[OSD([sQuery(id+"F8.wireOp",EDGE,"E15.16.9.0")])],"isStart":false})});
            var Q93;
            Q93=makeQuery(id+"F9.boolean.opBoolean","COPY",EDGE,{"derivedFrom":makeQuery(id+"F9.opExtrude","CAP_EDGE",EDGE,{"disambiguationData":[OSD([sQuery(id+"F8.wireOp",EDGE,"E15.12.9.0")])],"isStart":true})});
            var Q94;
            Q94=makeQuery(id+"F9.boolean.opBoolean","COPY",EDGE,{"derivedFrom":makeQuery(id+"F9.opExtrude","CAP_EDGE",EDGE,{"disambiguationData":[OSD([sQuery(id+"F8.wireOp",EDGE,"E15.1.9.0")])],"isStart":false})});
            var Q95;
            Q95=makeQuery(id+"F9.boolean.opBoolean","COPY",EDGE,{"derivedFrom":makeQuery(id+"F9.opExtrude","SWEPT_EDGE",EDGE,{"disambiguationData":[OSD([sQuery(id+"F8.wireOp",EDGE,"E15.12.10.0"),sQuery(id+"F8.wireOp",EDGE,"E15.16.10.0")])]})});
            var Q96;
            Q96=makeQuery(id+"F9.boolean.opBoolean","COPY",EDGE,{"derivedFrom":makeQuery(id+"F9.opExtrude","CAP_EDGE",EDGE,{"disambiguationData":[OSD([sQuery(id+"F8.wireOp",EDGE,"E15.20.8.0")])],"isStart":false})});
            var Q97;
            Q97=makeQuery(id+"F9.boolean.opBoolean","COPY",EDGE,{"derivedFrom":makeQuery(id+"F9.opExtrude","SWEPT_EDGE",EDGE,{"disambiguationData":[OSD([sQuery(id+"F8.wireOp",EDGE,"E15.12.10.0"),sQuery(id+"F8.wireOp",EDGE,"E15.20.10.0")])]})});
            var Q98;
            Q98=makeQuery(id+"F9.boolean.opBoolean","COPY",EDGE,{"derivedFrom":makeQuery(id+"F9.opExtrude","SWEPT_EDGE",EDGE,{"disambiguationData":[OSD([sQuery(id+"F8.wireOp",EDGE,"E15.8.10.0"),sQuery(id+"F8.wireOp",EDGE,"E15.16.10.0")])]})});
            var Q99;
            Q99=makeQuery(id+"F9.boolean.opBoolean","COPY",EDGE,{"derivedFrom":makeQuery(id+"F9.opExtrude","SWEPT_EDGE",EDGE,{"disambiguationData":[OSD([sQuery(id+"F8.wireOp",EDGE,"E15.1.10.0"),sQuery(id+"F8.wireOp",EDGE,"E15.20.10.0")])]})});
            var Q100;
            Q100=makeQuery(id+"F9.boolean.opBoolean","COPY",EDGE,{"derivedFrom":makeQuery(id+"F9.opExtrude","CAP_EDGE",EDGE,{"disambiguationData":[OSD([sQuery(id+"F8.wireOp",EDGE,"E15.12.8.0")])],"isStart":true})});
            var Q101;
            Q101=makeQuery(id+"F9.boolean.opBoolean","COPY",EDGE,{"derivedFrom":makeQuery(id+"F9.opExtrude","SWEPT_EDGE",EDGE,{"disambiguationData":[OSD([sQuery(id+"F8.wireOp",EDGE,"E15.4.9.0"),sQuery(id+"F8.wireOp",EDGE,"E15.8.9.0")])]})});
            var Q102;
            Q102=makeQuery(id+"F9.boolean.opBoolean","COPY",EDGE,{"derivedFrom":makeQuery(id+"F9.opExtrude","SWEPT_EDGE",EDGE,{"disambiguationData":[OSD([sQuery(id+"F8.wireOp",EDGE,"E10.1.1"),sQuery(id+"F8.wireOp",EDGE,"E10.1.7")])]})});
            var Q103;
            Q103=makeQuery(id+"F9.boolean.opBoolean","COPY",EDGE,{"derivedFrom":makeQuery(id+"F9.opExtrude","SWEPT_EDGE",EDGE,{"disambiguationData":[OSD([sQuery(id+"F8.wireOp",EDGE,"E10.1.5"),sQuery(id+"F8.wireOp",EDGE,"E10.1.7")])]})});
            var Q104;
            Q104=makeQuery(id+"F9.boolean.opBoolean","COPY",EDGE,{"derivedFrom":makeQuery(id+"F9.opExtrude","SWEPT_EDGE",EDGE,{"disambiguationData":[OSD([sQuery(id+"F8.wireOp",EDGE,"E10.2.3"),sQuery(id+"F8.wireOp",EDGE,"E10.2.6")])]})});
            var Q105;
            Q105=makeQuery(id+"F9.boolean.opBoolean","COPY",EDGE,{"derivedFrom":makeQuery(id+"F9.opExtrude","SWEPT_EDGE",EDGE,{"disambiguationData":[OSD([sQuery(id+"F8.wireOp",EDGE,"E10.2.5"),sQuery(id+"F8.wireOp",EDGE,"E10.2.7")])]})});
            var Q106;
            Q106=makeQuery(id+"F9.boolean.opBoolean","COPY",EDGE,{"derivedFrom":makeQuery(id+"F9.opExtrude","SWEPT_EDGE",EDGE,{"disambiguationData":[OSD([sQuery(id+"F8.wireOp",EDGE,"E10.2.5"),sQuery(id+"F8.wireOp",EDGE,"E10.2.6")])]})});
            var Q107;
            Q107=makeQuery(id+"F9.boolean.opBoolean","COPY",EDGE,{"derivedFrom":makeQuery(id+"F9.opExtrude","SWEPT_EDGE",EDGE,{"disambiguationData":[OSD([sQuery(id+"F8.wireOp",EDGE,"E11.4.3.0"),sQuery(id+"F8.wireOp",EDGE,"E11.8.3.0")])]})});
            var Q108;
            Q108=makeQuery(id+"F9.boolean.opBoolean","COPY",EDGE,{"derivedFrom":makeQuery(id+"F9.opExtrude","CAP_EDGE",EDGE,{"disambiguationData":[OSD([sQuery(id+"F8.wireOp",EDGE,"E12.12.5.0")])],"isStart":true})});
            var Q109;
            Q109=makeQuery(id+"F9.boolean.opBoolean","COPY",EDGE,{"derivedFrom":makeQuery(id+"F9.opExtrude","SWEPT_EDGE",EDGE,{"disambiguationData":[OSD([sQuery(id+"F8.wireOp",EDGE,"E11.1.4.0"),sQuery(id+"F8.wireOp",EDGE,"E11.4.4.0")])]})});
            var Q110;
            Q110=makeQuery(id+"F9.boolean.opBoolean","COPY",EDGE,{"derivedFrom":makeQuery(id+"F9.opExtrude","CAP_EDGE",EDGE,{"disambiguationData":[OSD([sQuery(id+"F8.wireOp",EDGE,"E12.20.5.0")])],"isStart":true})});
            var Q111;
            Q111=makeQuery(id+"F5.boolean.opBoolean","INTERSECT",EDGE,{"derivedFrom":[makeQuery(id+"F3.opExtrude","CAP_FACE",FACE,{"disambiguationData":[OSD([sQuery(id+"F0.wireOp",EDGE,"E1")])],"isStart":true}),makeQuery(id+"F5.opExtrude","SWEPT_FACE",FACE,{"disambiguationData":[OSD([sQuery(id+"F4.wireOp",EDGE,"E2")])]})]});
            var Q112;
            Q112=makeQuery(id+"F9.boolean.opBoolean","COPY",EDGE,{"derivedFrom":makeQuery(id+"F9.opExtrude","CAP_EDGE",EDGE,{"disambiguationData":[OSD([sQuery(id+"F8.wireOp",EDGE,"E13.1.6.0")])],"isStart":true})});
            var Q113;
            Q113=makeQuery(id+"F9.boolean.opBoolean","COPY",EDGE,{"derivedFrom":makeQuery(id+"F9.opExtrude","CAP_EDGE",EDGE,{"disambiguationData":[OSD([sQuery(id+"F8.wireOp",EDGE,"E13.1.6.0")])],"isStart":false})});
            var Q114;
            Q114=makeQuery(id+"F9.boolean.opBoolean","COPY",EDGE,{"derivedFrom":makeQuery(id+"F9.opExtrude","CAP_EDGE",EDGE,{"disambiguationData":[OSD([sQuery(id+"F8.wireOp",EDGE,"E12.16.5.0")])],"isStart":true})});
            var Q115;
            Q115=makeQuery(id+"F9.boolean.opBoolean","COPY",EDGE,{"derivedFrom":makeQuery(id+"F9.opExtrude","CAP_EDGE",EDGE,{"disambiguationData":[OSD([sQuery(id+"F8.wireOp",EDGE,"E11.4.3.0")])],"isStart":false})});
            var Q116;
            Q116=makeQuery(id+"F9.boolean.opBoolean","COPY",EDGE,{"derivedFrom":makeQuery(id+"F9.opExtrude","CAP_EDGE",EDGE,{"disambiguationData":[OSD([sQuery(id+"F8.wireOp",EDGE,"E14.1.7.0")])],"isStart":true})});
            var Q117;
            Q117=makeQuery(id+"F9.boolean.opBoolean","COPY",EDGE,{"derivedFrom":makeQuery(id+"F9.opExtrude","CAP_EDGE",EDGE,{"disambiguationData":[OSD([sQuery(id+"F8.wireOp",EDGE,"E15.4.8.0")])],"isStart":false})});
            var Q118;
            Q118=makeQuery(id+"F9.boolean.opBoolean","COPY",EDGE,{"derivedFrom":makeQuery(id+"F9.opExtrude","CAP_EDGE",EDGE,{"disambiguationData":[OSD([sQuery(id+"F8.wireOp",EDGE,"E15.8.9.0")])],"isStart":true})});
            var Q119;
            Q119=makeQuery(id+"F9.boolean.opBoolean","COPY",EDGE,{"derivedFrom":makeQuery(id+"F9.opExtrude","CAP_EDGE",EDGE,{"disambiguationData":[OSD([sQuery(id+"F8.wireOp",EDGE,"E13.8.6.0")])],"isStart":true})});
            var Q120;
            Q120=makeQuery(id+"F9.boolean.opBoolean","COPY",EDGE,{"derivedFrom":makeQuery(id+"F9.opExtrude","CAP_EDGE",EDGE,{"disambiguationData":[OSD([sQuery(id+"F8.wireOp",EDGE,"E12.1.5.0")])],"isStart":true})});
            var Q121;
            Q121=makeQuery(id+"F9.boolean.opBoolean","COPY",EDGE,{"derivedFrom":makeQuery(id+"F9.opExtrude","CAP_EDGE",EDGE,{"disambiguationData":[OSD([sQuery(id+"F8.wireOp",EDGE,"E13.12.6.0")])],"isStart":true})});
            var Q122;
            Q122=makeQuery(id+"F9.boolean.opBoolean","COPY",EDGE,{"derivedFrom":makeQuery(id+"F9.opExtrude","SWEPT_EDGE",EDGE,{"disambiguationData":[OSD([sQuery(id+"F8.wireOp",EDGE,"E12.1.5.0"),sQuery(id+"F8.wireOp",EDGE,"E12.4.5.0")])]})});
            var Q123;
            Q123=makeQuery(id+"F9.boolean.opBoolean","COPY",EDGE,{"derivedFrom":makeQuery(id+"F9.opExtrude","CAP_EDGE",EDGE,{"disambiguationData":[OSD([sQuery(id+"F8.wireOp",EDGE,"E11.4.4.0")])],"isStart":false})});
            var Q124;
            Q124=makeQuery(id+"F9.boolean.opBoolean","COPY",EDGE,{"derivedFrom":makeQuery(id+"F9.opExtrude","CAP_EDGE",EDGE,{"disambiguationData":[OSD([sQuery(id+"F8.wireOp",EDGE,"E7.filletArc")])],"isStart":false})});
            var Q125;
            Q125=makeQuery(id+"F9.boolean.opBoolean","COPY",EDGE,{"derivedFrom":makeQuery(id+"F9.opExtrude","CAP_EDGE",EDGE,{"disambiguationData":[OSD([sQuery(id+"F8.wireOp",EDGE,"E13.16.6.0")])],"isStart":false})});
            var Q126;
            Q126=makeQuery(id+"F9.boolean.opBoolean","COPY",EDGE,{"derivedFrom":makeQuery(id+"F9.opExtrude","CAP_EDGE",EDGE,{"disambiguationData":[OSD([sQuery(id+"F8.wireOp",EDGE,"E15.1.8.0")])],"isStart":true})});
            var Q127;
            Q127=makeQuery(id+"F9.boolean.opBoolean","COPY",EDGE,{"derivedFrom":makeQuery(id+"F9.opExtrude","CAP_EDGE",EDGE,{"disambiguationData":[OSD([sQuery(id+"F8.wireOp",EDGE,"E15.4.10.0")])],"isStart":false})});
            var Q128;
            Q128=makeQuery(id+"F9.boolean.opBoolean","COPY",EDGE,{"derivedFrom":makeQuery(id+"F9.opExtrude","CAP_EDGE",EDGE,{"disambiguationData":[OSD([sQuery(id+"F8.wireOp",EDGE,"E15.12.10.0")])],"isStart":true})});
            var Q129;
            Q129=makeQuery(id+"F9.boolean.opBoolean","COPY",EDGE,{"derivedFrom":makeQuery(id+"F9.opExtrude","SWEPT_EDGE",EDGE,{"disambiguationData":[OSD([sQuery(id+"F8.wireOp",EDGE,"E5"),sQuery(id+"F8.wireOp",EDGE,"E8.filletArc")])]})});
            var Q130;
            Q130=makeQuery(id+"F9.boolean.opBoolean","COPY",EDGE,{"derivedFrom":makeQuery(id+"F9.opExtrude","CAP_EDGE",EDGE,{"disambiguationData":[OSD([sQuery(id+"F8.wireOp",EDGE,"E10.2.7")])],"isStart":false})});
            var Q131;
            Q131=makeQuery(id+"F9.boolean.opBoolean","COPY",EDGE,{"derivedFrom":makeQuery(id+"F9.opExtrude","SWEPT_EDGE",EDGE,{"disambiguationData":[OSD([sQuery(id+"F8.wireOp",EDGE,"E13.4.6.0"),sQuery(id+"F8.wireOp",EDGE,"E13.8.6.0")])]})});
            var Q132;
            Q132=makeQuery(id+"F9.boolean.opBoolean","COPY",EDGE,{"derivedFrom":makeQuery(id+"F9.opExtrude","CAP_EDGE",EDGE,{"disambiguationData":[OSD([sQuery(id+"F8.wireOp",EDGE,"E14.8.7.0")])],"isStart":true})});
            var Q133;
            Q133=makeQuery(id+"F9.boolean.opBoolean","COPY",EDGE,{"derivedFrom":makeQuery(id+"F9.opExtrude","SWEPT_EDGE",EDGE,{"disambiguationData":[OSD([sQuery(id+"F8.wireOp",EDGE,"E11.8.3.0"),sQuery(id+"F8.wireOp",EDGE,"E11.16.3.0")])]})});
            var Q134;
            Q134=makeQuery(id+"F9.boolean.opBoolean","COPY",EDGE,{"derivedFrom":makeQuery(id+"F9.opExtrude","CAP_EDGE",EDGE,{"disambiguationData":[OSD([sQuery(id+"F8.wireOp",EDGE,"E14.16.7.0")])],"isStart":false})});
            var Q135;
            Q135=makeQuery(id+"F9.boolean.opBoolean","COPY",EDGE,{"derivedFrom":makeQuery(id+"F9.opExtrude","CAP_EDGE",EDGE,{"disambiguationData":[OSD([sQuery(id+"F8.wireOp",EDGE,"E11.20.4.0")])],"isStart":false})});
            var Q136;
            Q136=makeQuery(id+"F9.boolean.opBoolean","COPY",EDGE,{"derivedFrom":makeQuery(id+"F9.opExtrude","CAP_EDGE",EDGE,{"disambiguationData":[OSD([sQuery(id+"F8.wireOp",EDGE,"E10.1.1")])],"isStart":true})});
            var Q137;
            Q137=makeQuery(id+"F9.boolean.opBoolean","COPY",EDGE,{"derivedFrom":makeQuery(id+"F9.opExtrude","CAP_EDGE",EDGE,{"disambiguationData":[OSD([sQuery(id+"F8.wireOp",EDGE,"E11.16.4.0")])],"isStart":false})});
            var Q138;
            Q138=makeQuery(id+"F9.boolean.opBoolean","COPY",EDGE,{"derivedFrom":makeQuery(id+"F9.opExtrude","CAP_EDGE",EDGE,{"disambiguationData":[OSD([sQuery(id+"F8.wireOp",EDGE,"E10.1.3")])],"isStart":true})});
            var Q139;
            Q139=makeQuery(id+"F9.boolean.opBoolean","COPY",EDGE,{"derivedFrom":makeQuery(id+"F9.opExtrude","CAP_EDGE",EDGE,{"disambiguationData":[OSD([sQuery(id+"F8.wireOp",EDGE,"E13.4.6.0")])],"isStart":false})});
            var Q140;
            Q140=makeQuery(id+"F9.boolean.opBoolean","COPY",EDGE,{"derivedFrom":makeQuery(id+"F9.opExtrude","CAP_EDGE",EDGE,{"disambiguationData":[OSD([sQuery(id+"F8.wireOp",EDGE,"E12.4.5.0")])],"isStart":false})});
            var Q141;
            Q141=makeQuery(id+"F9.boolean.opBoolean","COPY",EDGE,{"derivedFrom":makeQuery(id+"F9.opExtrude","CAP_EDGE",EDGE,{"disambiguationData":[OSD([sQuery(id+"F8.wireOp",EDGE,"E7.filletArc")])],"isStart":true})});
            var Q142;
            Q142=makeQuery(id+"F9.boolean.opBoolean","COPY",EDGE,{"derivedFrom":makeQuery(id+"F9.opExtrude","CAP_EDGE",EDGE,{"disambiguationData":[OSD([sQuery(id+"F8.wireOp",EDGE,"E11.4.4.0")])],"isStart":true})});
            var Q143;
            Q143=makeQuery(id+"F9.boolean.opBoolean","COPY",EDGE,{"derivedFrom":makeQuery(id+"F9.opExtrude","CAP_EDGE",EDGE,{"disambiguationData":[OSD([sQuery(id+"F8.wireOp",EDGE,"E11.16.4.0")])],"isStart":true})});
            var Q144;
            Q144=makeQuery(id+"F9.boolean.opBoolean","COPY",EDGE,{"derivedFrom":makeQuery(id+"F9.opExtrude","CAP_EDGE",EDGE,{"disambiguationData":[OSD([sQuery(id+"F8.wireOp",EDGE,"E11.20.4.0")])],"isStart":true})});
            var Q145;
            Q145=makeQuery(id+"F9.boolean.opBoolean","COPY",EDGE,{"derivedFrom":makeQuery(id+"F9.opExtrude","CAP_EDGE",EDGE,{"disambiguationData":[OSD([sQuery(id+"F8.wireOp",EDGE,"E10.2.7")])],"isStart":true})});
            var Q146;
            Q146=makeQuery(id+"F9.boolean.opBoolean","COPY",EDGE,{"derivedFrom":makeQuery(id+"F9.opExtrude","CAP_EDGE",EDGE,{"disambiguationData":[OSD([sQuery(id+"F8.wireOp",EDGE,"E11.1.3.0")])],"isStart":true})});
            var Q147;
            Q147=makeQuery(id+"F9.boolean.opBoolean","COPY",EDGE,{"derivedFrom":makeQuery(id+"F9.opExtrude","CAP_EDGE",EDGE,{"disambiguationData":[OSD([sQuery(id+"F8.wireOp",EDGE,"E11.4.3.0")])],"isStart":true})});
            var Q148;
            Q148=makeQuery(id+"F9.boolean.opBoolean","COPY",EDGE,{"derivedFrom":makeQuery(id+"F9.opExtrude","SWEPT_EDGE",EDGE,{"disambiguationData":[OSD([sQuery(id+"F8.wireOp",EDGE,"E6"),sQuery(id+"F8.wireOp",EDGE,"E7.filletArc")])]})});
            var Q149;
            Q149=makeQuery(id+"F9.boolean.opBoolean","COPY",EDGE,{"derivedFrom":makeQuery(id+"F9.opExtrude","CAP_EDGE",EDGE,{"disambiguationData":[OSD([sQuery(id+"F8.wireOp",EDGE,"E11.16.3.0")])],"isStart":true})});
            var Q150;
            Q150=makeQuery(id+"F9.boolean.opBoolean","COPY",EDGE,{"derivedFrom":makeQuery(id+"F9.opExtrude","CAP_EDGE",EDGE,{"disambiguationData":[OSD([sQuery(id+"F8.wireOp",EDGE,"E11.20.3.0")])],"isStart":true})});
            var Q151;
            Q151=makeQuery(id+"F9.boolean.opBoolean","COPY",EDGE,{"derivedFrom":makeQuery(id+"F9.opExtrude","SWEPT_EDGE",EDGE,{"disambiguationData":[OSD([sQuery(id+"F8.wireOp",EDGE,"E4"),sQuery(id+"F8.wireOp",EDGE,"E9.filletArc")])]})});
            var Q152;
            Q152=makeQuery(id+"F9.boolean.opBoolean","COPY",EDGE,{"derivedFrom":makeQuery(id+"F9.opExtrude","SWEPT_EDGE",EDGE,{"disambiguationData":[OSD([sQuery(id+"F8.wireOp",EDGE,"E5"),sQuery(id+"F8.wireOp",EDGE,"E7.filletArc")])]})});
            var Q153;
            Q153=makeQuery(id+"F9.boolean.opBoolean","COPY",EDGE,{"derivedFrom":makeQuery(id+"F9.opExtrude","CAP_EDGE",EDGE,{"disambiguationData":[OSD([sQuery(id+"F8.wireOp",EDGE,"E15.4.11.0")])],"isStart":true})});
            var Q154;
            Q154=makeQuery(id+"F9.boolean.opBoolean","COPY",EDGE,{"derivedFrom":makeQuery(id+"F9.opExtrude","SWEPT_EDGE",EDGE,{"disambiguationData":[OSD([sQuery(id+"F8.wireOp",EDGE,"E11.8.4.0"),sQuery(id+"F8.wireOp",EDGE,"E11.16.4.0")])]})});
            var Q155;
            Q155=makeQuery(id+"F9.boolean.opBoolean","COPY",EDGE,{"derivedFrom":makeQuery(id+"F9.opExtrude","CAP_EDGE",EDGE,{"disambiguationData":[OSD([sQuery(id+"F8.wireOp",EDGE,"E10.2.2")])],"isStart":true})});
            var Q156;
            Q156=makeQuery(id+"F9.boolean.opBoolean","COPY",EDGE,{"derivedFrom":makeQuery(id+"F9.opExtrude","SWEPT_EDGE",EDGE,{"disambiguationData":[OSD([sQuery(id+"F8.wireOp",EDGE,"E11.1.4.0"),sQuery(id+"F8.wireOp",EDGE,"E11.20.4.0")])]})});
            var Q157;
            Q157=makeQuery(id+"F9.boolean.opBoolean","COPY",EDGE,{"derivedFrom":makeQuery(id+"F9.opExtrude","CAP_EDGE",EDGE,{"disambiguationData":[OSD([sQuery(id+"F8.wireOp",EDGE,"E10.1.7")])],"isStart":true})});
            var Q158;
            Q158=makeQuery(id+"F9.boolean.opBoolean","COPY",EDGE,{"derivedFrom":makeQuery(id+"F9.opExtrude","SWEPT_EDGE",EDGE,{"disambiguationData":[OSD([sQuery(id+"F8.wireOp",EDGE,"E15.12.8.0"),sQuery(id+"F8.wireOp",EDGE,"E15.16.8.0")])]})});
            var Q159;
            Q159=makeQuery(id+"F9.boolean.opBoolean","COPY",EDGE,{"derivedFrom":makeQuery(id+"F9.opExtrude","CAP_EDGE",EDGE,{"disambiguationData":[OSD([sQuery(id+"F8.wireOp",EDGE,"E10.1.6")])],"isStart":true})});
            var Q160;
            Q160=makeQuery(id+"F9.boolean.opBoolean","COPY",EDGE,{"derivedFrom":makeQuery(id+"F9.opExtrude","SWEPT_EDGE",EDGE,{"disambiguationData":[OSD([sQuery(id+"F8.wireOp",EDGE,"E14.12.7.0"),sQuery(id+"F8.wireOp",EDGE,"E14.16.7.0")])]})});
            var Q161;
            Q161=makeQuery(id+"F9.boolean.opBoolean","COPY",EDGE,{"derivedFrom":makeQuery(id+"F9.opExtrude","SWEPT_EDGE",EDGE,{"disambiguationData":[OSD([sQuery(id+"F8.wireOp",EDGE,"E14.12.7.0"),sQuery(id+"F8.wireOp",EDGE,"E14.20.7.0")])]})});
            var Q162;
            Q162=makeQuery(id+"F9.boolean.opBoolean","COPY",EDGE,{"derivedFrom":makeQuery(id+"F9.opExtrude","CAP_EDGE",EDGE,{"disambiguationData":[OSD([sQuery(id+"F8.wireOp",EDGE,"E10.1.2")])],"isStart":true})});
            var Q163;
            Q163=makeQuery(id+"F9.boolean.opBoolean","COPY",EDGE,{"derivedFrom":makeQuery(id+"F9.opExtrude","SWEPT_EDGE",EDGE,{"disambiguationData":[OSD([sQuery(id+"F8.wireOp",EDGE,"E14.4.7.0"),sQuery(id+"F8.wireOp",EDGE,"E14.8.7.0")])]})});
            var Q164;
            Q164=makeQuery(id+"F9.boolean.opBoolean","COPY",EDGE,{"derivedFrom":makeQuery(id+"F9.opExtrude","CAP_EDGE",EDGE,{"disambiguationData":[OSD([sQuery(id+"F8.wireOp",EDGE,"E8.filletArc")])],"isStart":true})});
            var Q165;
            Q165=makeQuery(id+"F9.boolean.opBoolean","COPY",EDGE,{"derivedFrom":makeQuery(id+"F9.opExtrude","CAP_EDGE",EDGE,{"disambiguationData":[OSD([sQuery(id+"F8.wireOp",EDGE,"E15.16.11.0")])],"isStart":true})});
            var Q166;
            Q166=makeQuery(id+"F9.boolean.opBoolean","COPY",EDGE,{"derivedFrom":makeQuery(id+"F9.opExtrude","SWEPT_EDGE",EDGE,{"disambiguationData":[OSD([sQuery(id+"F8.wireOp",EDGE,"E13.12.6.0"),sQuery(id+"F8.wireOp",EDGE,"E13.20.6.0")])]})});
            var Q167;
            Q167=makeQuery(id+"F9.boolean.opBoolean","COPY",EDGE,{"derivedFrom":makeQuery(id+"F9.opExtrude","SWEPT_EDGE",EDGE,{"disambiguationData":[OSD([sQuery(id+"F8.wireOp",EDGE,"E13.12.6.0"),sQuery(id+"F8.wireOp",EDGE,"E13.16.6.0")])]})});
            var Q168;
            Q168=makeQuery(id+"F9.boolean.opBoolean","COPY",EDGE,{"derivedFrom":makeQuery(id+"F9.opExtrude","SWEPT_EDGE",EDGE,{"disambiguationData":[OSD([sQuery(id+"F8.wireOp",EDGE,"E14.1.7.0"),sQuery(id+"F8.wireOp",EDGE,"E14.20.7.0")])]})});
            var Q169;
            Q169=makeQuery(id+"F9.boolean.opBoolean","COPY",EDGE,{"derivedFrom":makeQuery(id+"F9.opExtrude","CAP_EDGE",EDGE,{"disambiguationData":[OSD([sQuery(id+"F8.wireOp",EDGE,"E15.20.9.0")])],"isStart":true})});
            var Q170;
            Q170=makeQuery(id+"F9.boolean.opBoolean","COPY",EDGE,{"derivedFrom":makeQuery(id+"F9.opExtrude","SWEPT_EDGE",EDGE,{"disambiguationData":[OSD([sQuery(id+"F8.wireOp",EDGE,"E15.1.11.0"),sQuery(id+"F8.wireOp",EDGE,"E15.4.11.0")])]})});
            var Q171;
            Q171=makeQuery(id+"F9.boolean.opBoolean","COPY",EDGE,{"derivedFrom":makeQuery(id+"F9.opExtrude","CAP_EDGE",EDGE,{"disambiguationData":[OSD([sQuery(id+"F8.wireOp",EDGE,"E15.1.9.0")])],"isStart":true})});
            var Q172;
            Q172=makeQuery(id+"F9.boolean.opBoolean","COPY",EDGE,{"derivedFrom":makeQuery(id+"F9.opExtrude","CAP_EDGE",EDGE,{"disambiguationData":[OSD([sQuery(id+"F8.wireOp",EDGE,"E15.20.8.0")])],"isStart":true})});
            var Q173;
            Q173=makeQuery(id+"F9.boolean.opBoolean","COPY",EDGE,{"derivedFrom":makeQuery(id+"F9.opExtrude","CAP_EDGE",EDGE,{"disambiguationData":[OSD([sQuery(id+"F8.wireOp",EDGE,"E6")])],"isStart":false})});
            var Q174;
            Q174=makeQuery(id+"F9.boolean.opBoolean","COPY",EDGE,{"derivedFrom":makeQuery(id+"F9.opExtrude","CAP_EDGE",EDGE,{"disambiguationData":[OSD([sQuery(id+"F8.wireOp",EDGE,"E15.16.8.0")])],"isStart":true})});
            var Q175;
            Q175=makeQuery(id+"F9.boolean.opBoolean","COPY",EDGE,{"derivedFrom":makeQuery(id+"F9.opExtrude","SWEPT_EDGE",EDGE,{"disambiguationData":[OSD([sQuery(id+"F8.wireOp",EDGE,"E6"),sQuery(id+"F8.wireOp",EDGE,"E9.filletArc")])]})});
            var Q176;
            Q176=makeQuery(id+"F9.boolean.opBoolean","COPY",EDGE,{"derivedFrom":makeQuery(id+"F9.opExtrude","CAP_EDGE",EDGE,{"disambiguationData":[OSD([sQuery(id+"F8.wireOp",EDGE,"E15.4.8.0")])],"isStart":true})});
            var Q177;
            Q177=makeQuery(id+"F9.boolean.opBoolean","COPY",EDGE,{"derivedFrom":makeQuery(id+"F9.opExtrude","SWEPT_EDGE",EDGE,{"disambiguationData":[OSD([sQuery(id+"F8.wireOp",EDGE,"E13.1.6.0"),sQuery(id+"F8.wireOp",EDGE,"E13.20.6.0")])]})});
            var Q178;
            Q178=makeQuery(id+"F9.boolean.opBoolean","COPY",EDGE,{"derivedFrom":makeQuery(id+"F9.opExtrude","SWEPT_EDGE",EDGE,{"disambiguationData":[OSD([sQuery(id+"F8.wireOp",EDGE,"E15.4.11.0"),sQuery(id+"F8.wireOp",EDGE,"E15.8.11.0")])]})});
            var Q179;
            Q179=makeQuery(id+"F9.boolean.opBoolean","COPY",EDGE,{"derivedFrom":makeQuery(id+"F9.opExtrude","CAP_EDGE",EDGE,{"disambiguationData":[OSD([sQuery(id+"F8.wireOp",EDGE,"E15.4.9.0")])],"isStart":true})});
            var Q180;
            Q180=makeQuery(id+"F9.boolean.opBoolean","COPY",EDGE,{"derivedFrom":makeQuery(id+"F9.opExtrude","SWEPT_EDGE",EDGE,{"disambiguationData":[OSD([sQuery(id+"F8.wireOp",EDGE,"E10.1.1"),sQuery(id+"F8.wireOp",EDGE,"E10.1.2")])]})});
            var Q181;
            Q181=makeQuery(id+"F9.boolean.opBoolean","COPY",EDGE,{"derivedFrom":makeQuery(id+"F9.opExtrude","SWEPT_EDGE",EDGE,{"disambiguationData":[OSD([sQuery(id+"F8.wireOp",EDGE,"E10.1.2"),sQuery(id+"F8.wireOp",EDGE,"E10.1.3")])]})});
            var Q182;
            Q182=makeQuery(id+"F9.boolean.opBoolean","COPY",EDGE,{"derivedFrom":makeQuery(id+"F9.opExtrude","SWEPT_EDGE",EDGE,{"disambiguationData":[OSD([sQuery(id+"F8.wireOp",EDGE,"E10.1.3"),sQuery(id+"F8.wireOp",EDGE,"E10.1.6")])]})});
            var Q183;
            Q183=makeQuery(id+"F9.boolean.opBoolean","COPY",EDGE,{"derivedFrom":makeQuery(id+"F9.opExtrude","SWEPT_EDGE",EDGE,{"disambiguationData":[OSD([sQuery(id+"F8.wireOp",EDGE,"E10.1.5"),sQuery(id+"F8.wireOp",EDGE,"E10.1.6")])]})});
            var Q184;
            Q184=makeQuery(id+"F9.boolean.opBoolean","COPY",EDGE,{"derivedFrom":makeQuery(id+"F9.opExtrude","SWEPT_EDGE",EDGE,{"disambiguationData":[OSD([sQuery(id+"F8.wireOp",EDGE,"E10.2.1"),sQuery(id+"F8.wireOp",EDGE,"E10.2.7")])]})});
            var Q185;
            Q185=makeQuery(id+"F9.boolean.opBoolean","COPY",EDGE,{"derivedFrom":makeQuery(id+"F9.opExtrude","SWEPT_EDGE",EDGE,{"disambiguationData":[OSD([sQuery(id+"F8.wireOp",EDGE,"E10.2.1"),sQuery(id+"F8.wireOp",EDGE,"E10.2.2")])]})});
            var Q186;
            Q186=makeQuery(id+"F9.boolean.opBoolean","COPY",EDGE,{"derivedFrom":makeQuery(id+"F9.opExtrude","SWEPT_EDGE",EDGE,{"disambiguationData":[OSD([sQuery(id+"F8.wireOp",EDGE,"E10.2.2"),sQuery(id+"F8.wireOp",EDGE,"E10.2.3")])]})});
            var Q187;
            Q187=makeQuery(id+"F9.boolean.opBoolean","COPY",EDGE,{"derivedFrom":makeQuery(id+"F9.opExtrude","SWEPT_EDGE",EDGE,{"disambiguationData":[OSD([sQuery(id+"F8.wireOp",EDGE,"E15.12.9.0"),sQuery(id+"F8.wireOp",EDGE,"E15.16.9.0")])]})});
            var Q188;
            Q188=makeQuery(id+"F9.boolean.opBoolean","COPY",EDGE,{"derivedFrom":makeQuery(id+"F9.opExtrude","SWEPT_EDGE",EDGE,{"disambiguationData":[OSD([sQuery(id+"F8.wireOp",EDGE,"E11.1.3.0"),sQuery(id+"F8.wireOp",EDGE,"E11.20.3.0")])]})});
            var Q189;
            Q189=makeQuery(id+"F9.boolean.opBoolean","COPY",EDGE,{"derivedFrom":makeQuery(id+"F9.opExtrude","SWEPT_EDGE",EDGE,{"disambiguationData":[OSD([sQuery(id+"F8.wireOp",EDGE,"E11.1.3.0"),sQuery(id+"F8.wireOp",EDGE,"E11.4.3.0")])]})});
            var Q190;
            Q190=makeQuery(id+"F9.boolean.opBoolean","COPY",EDGE,{"derivedFrom":makeQuery(id+"F9.opExtrude","SWEPT_EDGE",EDGE,{"disambiguationData":[OSD([sQuery(id+"F8.wireOp",EDGE,"E14.8.7.0"),sQuery(id+"F8.wireOp",EDGE,"E14.16.7.0")])]})});
            var Q191;
            Q191=makeQuery(id+"F9.boolean.opBoolean","COPY",EDGE,{"derivedFrom":makeQuery(id+"F9.opExtrude","CAP_EDGE",EDGE,{"disambiguationData":[OSD([sQuery(id+"F8.wireOp",EDGE,"E13.20.6.0")])],"isStart":true})});
            var Q192;
            Q192=makeQuery(id+"F9.boolean.opBoolean","COPY",EDGE,{"derivedFrom":makeQuery(id+"F9.opExtrude","SWEPT_EDGE",EDGE,{"disambiguationData":[OSD([sQuery(id+"F8.wireOp",EDGE,"E15.8.8.0"),sQuery(id+"F8.wireOp",EDGE,"E15.16.8.0")])]})});
            var Q193;
            Q193=makeQuery(id+"F9.boolean.opBoolean","COPY",EDGE,{"derivedFrom":makeQuery(id+"F9.opExtrude","CAP_EDGE",EDGE,{"disambiguationData":[OSD([sQuery(id+"F8.wireOp",EDGE,"E15.16.9.0")])],"isStart":true})});
            var Q194;
            Q194=makeQuery(id+"F9.boolean.opBoolean","COPY",EDGE,{"derivedFrom":makeQuery(id+"F9.opExtrude","SWEPT_EDGE",EDGE,{"disambiguationData":[OSD([sQuery(id+"F8.wireOp",EDGE,"E15.12.11.0"),sQuery(id+"F8.wireOp",EDGE,"E15.20.11.0")])]})});
            var Q195;
            Q195=makeQuery(id+"F9.boolean.opBoolean","COPY",EDGE,{"derivedFrom":makeQuery(id+"F9.opExtrude","SWEPT_EDGE",EDGE,{"disambiguationData":[OSD([sQuery(id+"F8.wireOp",EDGE,"E15.1.8.0"),sQuery(id+"F8.wireOp",EDGE,"E15.20.8.0")])]})});
            var Q196;
            Q196=makeQuery(id+"F9.boolean.opBoolean","COPY",EDGE,{"derivedFrom":makeQuery(id+"F9.opExtrude","CAP_EDGE",EDGE,{"disambiguationData":[OSD([sQuery(id+"F8.wireOp",EDGE,"E14.12.7.0")])],"isStart":true})});
            var Q197;
            Q197=makeQuery(id+"F9.boolean.opBoolean","COPY",EDGE,{"derivedFrom":makeQuery(id+"F9.opExtrude","SWEPT_EDGE",EDGE,{"disambiguationData":[OSD([sQuery(id+"F8.wireOp",EDGE,"E13.1.6.0"),sQuery(id+"F8.wireOp",EDGE,"E13.4.6.0")])]})});
            var Q198;
            Q198=makeQuery(id+"F9.boolean.opBoolean","COPY",EDGE,{"derivedFrom":makeQuery(id+"F9.opExtrude","SWEPT_EDGE",EDGE,{"disambiguationData":[OSD([sQuery(id+"F8.wireOp",EDGE,"E11.12.3.0"),sQuery(id+"F8.wireOp",EDGE,"E11.20.3.0")])]})});
            var Q199;
            Q199=makeQuery(id+"F9.boolean.opBoolean","COPY",EDGE,{"derivedFrom":makeQuery(id+"F9.opExtrude","CAP_EDGE",EDGE,{"disambiguationData":[OSD([sQuery(id+"F8.wireOp",EDGE,"E13.16.6.0")])],"isStart":true})});
            var Q200;
            Q200=makeQuery(id+"F9.boolean.opBoolean","COPY",EDGE,{"derivedFrom":makeQuery(id+"F9.opExtrude","CAP_EDGE",EDGE,{"disambiguationData":[OSD([sQuery(id+"F8.wireOp",EDGE,"E14.20.7.0")])],"isStart":true})});
            var Q201;
            Q201=makeQuery(id+"F9.boolean.opBoolean","COPY",EDGE,{"derivedFrom":makeQuery(id+"F9.opExtrude","SWEPT_EDGE",EDGE,{"disambiguationData":[OSD([sQuery(id+"F8.wireOp",EDGE,"E15.8.9.0"),sQuery(id+"F8.wireOp",EDGE,"E15.16.9.0")])]})});
            var Q202;
            Q202=makeQuery(id+"F9.boolean.opBoolean","COPY",EDGE,{"derivedFrom":makeQuery(id+"F9.opExtrude","CAP_EDGE",EDGE,{"disambiguationData":[OSD([sQuery(id+"F8.wireOp",EDGE,"E12.4.5.0")])],"isStart":true})});
            var Q203;
            Q203=makeQuery(id+"F9.boolean.opBoolean","COPY",EDGE,{"derivedFrom":makeQuery(id+"F9.opExtrude","CAP_EDGE",EDGE,{"disambiguationData":[OSD([sQuery(id+"F8.wireOp",EDGE,"E15.8.10.0")])],"isStart":true})});
            var Q204;
            Q204=makeQuery(id+"F9.boolean.opBoolean","COPY",EDGE,{"derivedFrom":makeQuery(id+"F9.opExtrude","CAP_EDGE",EDGE,{"disambiguationData":[OSD([sQuery(id+"F8.wireOp",EDGE,"E15.8.10.0")])],"isStart":false})});
            var Q205;
            Q205=makeQuery(id+"F9.boolean.opBoolean","COPY",EDGE,{"derivedFrom":makeQuery(id+"F9.opExtrude","SWEPT_EDGE",EDGE,{"disambiguationData":[OSD([sQuery(id+"F8.wireOp",EDGE,"E15.1.8.0"),sQuery(id+"F8.wireOp",EDGE,"E15.4.8.0")])]})});
            var Q206;
            Q206=makeQuery(id+"F9.boolean.opBoolean","COPY",EDGE,{"derivedFrom":makeQuery(id+"F9.opExtrude","SWEPT_EDGE",EDGE,{"disambiguationData":[OSD([sQuery(id+"F8.wireOp",EDGE,"E15.1.9.0"),sQuery(id+"F8.wireOp",EDGE,"E15.4.9.0")])]})});
            var Q207;
            Q207=makeQuery(id+"F9.boolean.opBoolean","COPY",EDGE,{"derivedFrom":makeQuery(id+"F9.opExtrude","CAP_EDGE",EDGE,{"disambiguationData":[OSD([sQuery(id+"F8.wireOp",EDGE,"E14.4.7.0")])],"isStart":true})});
            var Q208;
            Q208=makeQuery(id+"F9.boolean.opBoolean","COPY",EDGE,{"derivedFrom":makeQuery(id+"F9.opExtrude","CAP_EDGE",EDGE,{"disambiguationData":[OSD([sQuery(id+"F8.wireOp",EDGE,"E14.4.7.0")])],"isStart":false})});
            var Q209;
            Q209=makeQuery(id+"F9.boolean.opBoolean","COPY",EDGE,{"derivedFrom":makeQuery(id+"F9.opExtrude","CAP_EDGE",EDGE,{"disambiguationData":[OSD([sQuery(id+"F8.wireOp",EDGE,"E15.16.10.0")])],"isStart":true})});
            var Q210;
            Q210=makeQuery(id+"F9.boolean.opBoolean","COPY",EDGE,{"derivedFrom":makeQuery(id+"F9.opExtrude","SWEPT_EDGE",EDGE,{"disambiguationData":[OSD([sQuery(id+"F8.wireOp",EDGE,"E15.1.9.0"),sQuery(id+"F8.wireOp",EDGE,"E15.20.9.0")])]})});
            var Q211;
            Q211=makeQuery(id+"F5.opExtrude","CAP_EDGE",EDGE,{"disambiguationData":[OSD([sQuery(id+"F4.wireOp",EDGE,"E2")])],"isStart":false});
            var Q212;
            Q212=makeQuery(id+"F9.boolean.opBoolean","COPY",EDGE,{"derivedFrom":makeQuery(id+"F9.opExtrude","SWEPT_EDGE",EDGE,{"disambiguationData":[OSD([sQuery(id+"F8.wireOp",EDGE,"E15.4.8.0"),sQuery(id+"F8.wireOp",EDGE,"E15.8.8.0")])]})});
            var Q213;
            Q213=makeQuery(id+"F9.boolean.opBoolean","COPY",EDGE,{"derivedFrom":makeQuery(id+"F9.opExtrude","CAP_EDGE",EDGE,{"disambiguationData":[OSD([sQuery(id+"F8.wireOp",EDGE,"E15.20.10.0")])],"isStart":true})});
            var Q214;
            Q214=makeQuery(id+"F9.boolean.opBoolean","COPY",EDGE,{"derivedFrom":makeQuery(id+"F9.opExtrude","CAP_EDGE",EDGE,{"disambiguationData":[OSD([sQuery(id+"F8.wireOp",EDGE,"E9.filletArc")])],"isStart":true})});
            var Q215;
            Q215=makeQuery(id+"F9.boolean.opBoolean","COPY",EDGE,{"derivedFrom":makeQuery(id+"F9.opExtrude","CAP_EDGE",EDGE,{"disambiguationData":[OSD([sQuery(id+"F8.wireOp",EDGE,"E13.4.6.0")])],"isStart":true})});
            var Q216;
            Q216=makeQuery(id+"F9.boolean.opBoolean","COPY",EDGE,{"derivedFrom":makeQuery(id+"F9.opExtrude","SWEPT_EDGE",EDGE,{"disambiguationData":[OSD([sQuery(id+"F8.wireOp",EDGE,"E15.8.11.0"),sQuery(id+"F8.wireOp",EDGE,"E15.16.11.0")])]})});
            var Q217;
            Q217=makeQuery(id+"F9.boolean.opBoolean","COPY",EDGE,{"derivedFrom":makeQuery(id+"F9.opExtrude","SWEPT_EDGE",EDGE,{"disambiguationData":[OSD([sQuery(id+"F8.wireOp",EDGE,"E11.4.4.0"),sQuery(id+"F8.wireOp",EDGE,"E11.8.4.0")])]})});
            var Q218;
            Q218=makeQuery(id+"F9.boolean.opBoolean","COPY",EDGE,{"derivedFrom":makeQuery(id+"F9.opExtrude","SWEPT_EDGE",EDGE,{"disambiguationData":[OSD([sQuery(id+"F8.wireOp",EDGE,"E15.1.11.0"),sQuery(id+"F8.wireOp",EDGE,"E15.20.11.0")])]})});
            var Q219;
            Q219=makeQuery(id+"F9.boolean.opBoolean","COPY",EDGE,{"derivedFrom":makeQuery(id+"F9.opExtrude","CAP_EDGE",EDGE,{"disambiguationData":[OSD([sQuery(id+"F8.wireOp",EDGE,"E14.16.7.0")])],"isStart":true})});
            var Q220;
            Q220=makeQuery(id+"F9.boolean.opBoolean","COPY",EDGE,{"derivedFrom":makeQuery(id+"F9.opExtrude","SWEPT_EDGE",EDGE,{"disambiguationData":[OSD([sQuery(id+"F8.wireOp",EDGE,"E15.4.10.0"),sQuery(id+"F8.wireOp",EDGE,"E15.8.10.0")])]})});
            var Q221;
            Q221=makeQuery(id+"F9.boolean.opBoolean","COPY",EDGE,{"derivedFrom":makeQuery(id+"F9.opExtrude","CAP_EDGE",EDGE,{"disambiguationData":[OSD([sQuery(id+"F8.wireOp",EDGE,"E15.4.10.0")])],"isStart":true})});
            var Q222;
            Q222=makeQuery(id+"F9.boolean.opBoolean","COPY",EDGE,{"derivedFrom":makeQuery(id+"F9.opExtrude","SWEPT_EDGE",EDGE,{"disambiguationData":[OSD([sQuery(id+"F8.wireOp",EDGE,"E15.1.10.0"),sQuery(id+"F8.wireOp",EDGE,"E15.4.10.0")])]})});
            var Q223;
            Q223=makeQuery(id+"F9.boolean.opBoolean","COPY",EDGE,{"derivedFrom":makeQuery(id+"F9.opExtrude","SWEPT_EDGE",EDGE,{"disambiguationData":[OSD([sQuery(id+"F8.wireOp",EDGE,"E14.1.7.0"),sQuery(id+"F8.wireOp",EDGE,"E14.4.7.0")])]})});
            fillet(context, id + "F10", {"entities" : qUnion([Q0, Q1, Q2, Q3, Q4, Q5, Q6, Q7, Q8, Q9, Q10, Q11, Q12, Q13, Q14, Q15, Q16, Q17, Q18, Q19, Q20, Q21, Q22, Q23, Q24, Q25, Q26, Q27, Q28, Q29, Q30, Q31, Q32, Q33, Q34, Q35, Q36, Q37, Q38, Q39, Q40, Q41, Q42, Q43, Q44, Q45, Q46, Q47, Q48, Q49, Q50, Q51, Q52, Q53, Q54, Q55, Q56, Q57, Q58, Q59, Q60, Q61, Q62, Q63, Q64, Q65, Q66, Q67, Q68, Q69, Q70, Q71, Q72, Q73, Q74, Q75, Q76, Q77, Q78, Q79, Q80, Q81, Q82, Q83, Q84, Q85, Q86, Q87, Q88, Q89, Q90, Q91, Q92, Q93, Q94, Q95, Q96, Q97, Q98, Q99, Q100, Q101, Q102, Q103, Q104, Q105, Q106, Q107, Q108, Q109, Q110, Q111, Q112, Q113, Q114, Q115, Q116, Q117, Q118, Q119, Q120, Q121, Q122, Q123, Q124, Q125, Q126, Q127, Q128, Q129, Q130, Q131, Q132, Q133, Q134, Q135, Q136, Q137, Q138, Q139, Q140, Q141, Q142, Q143, Q144, Q145, Q146, Q147, Q148, Q149, Q150, Q151, Q152, Q153, Q154, Q155, Q156, Q157, Q158, Q159, Q160, Q161, Q162, Q163, Q164, Q165, Q166, Q167, Q168, Q169, Q170, Q171, Q172, Q173, Q174, Q175, Q176, Q177, Q178, Q179, Q180, Q181, Q182, Q183, Q184, Q185, Q186, Q187, Q188, Q189, Q190, Q191, Q192, Q193, Q194, Q195, Q196, Q197, Q198, Q199, Q200, Q201, Q202, Q203, Q204, Q205, Q206, Q207, Q208, Q209, Q210, Q211, Q212, Q213, Q214, Q215, Q216, Q217, Q218, Q219, Q220, Q221, Q222, Q223]), "radius" : 1 * mm, "tangentPropagation" : true, "allowEdgeOverflow" : false});
        }
        {
            var Q0;
            Q0=qCreatedBy(makeId("Top.planeOp"),FACE);
            var sketch = newSketch(context, id + "F11", { "sketchPlane" : qUnion([Q0])});
            skCircle(sketch, "E16", {"center": v(0, 0) * mm, "radius": 4.39 * mm});
            skCircle(sketch, "E17", {"center": v(0, 0) * mm, "radius": 44.55 * mm});
            skSolve(sketch);
        }
        {
            var Q0;
            Q0 = qSketchRegion(id + "F11", true);
            extrude(context, id + "F12", {"entities" : qUnion([Q0]), "operationType" : NewBodyOperationType.REMOVE, "oppositeDirection" : true, "depth" : 12 * mm, "offsetDistance" : 25 * mm, "symmetric" : true});
        }
    });
